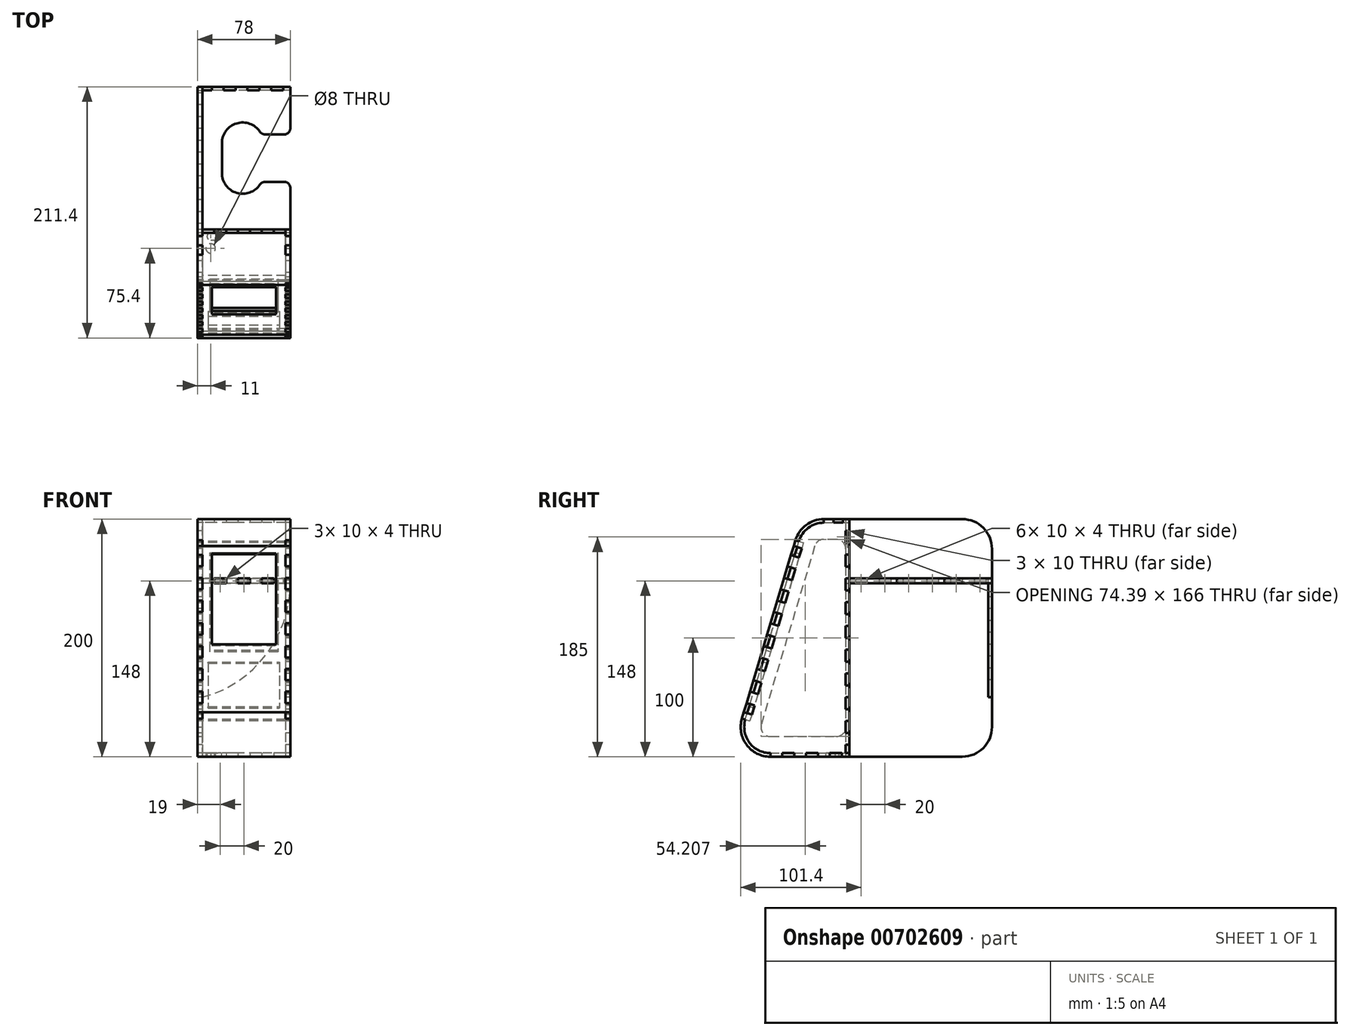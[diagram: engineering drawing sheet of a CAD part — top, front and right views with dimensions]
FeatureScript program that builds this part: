
annotation { "Feature Type Name" : "Feature", "Feature Type Description" : "" }
export const myFeature = defineFeature(function(context is Context, id is Id, definition is map)
    precondition{}
    {
        {
            var Q0;
            Q0=qCreatedBy(makeId("Right.planeOp"),FACE);
            var sketch = newSketch(context, id + "F0", { "sketchPlane" : qUnion([Q0])});
            skLineSegment(sketch, "E0", {"start": v(0, 0) * mm, "end": v(-66.4, 0) * mm});
            skLineSegment(sketch, "E1", {"start": v(-90.34, 32.18) * mm, "end": v(-87.13, 42.92) * mm});
            skLineSegment(sketch, "E2", {"start": v(-21.4, 200) * mm, "end": v(0, 200) * mm});
            skLineSegment(sketch, "E3", {"start": v(0, 200) * mm, "end": v(0, 0) * mm});
            skLineSegment(sketch, "E4", {"start": v(0, 0) * mm, "end": v(95, 0) * mm});
            skLineSegment(sketch, "E5", {"start": v(120, 25) * mm, "end": v(120, 175) * mm});
            skLineSegment(sketch, "E6", {"start": v(95, 200) * mm, "end": v(0, 200) * mm});
            skLineSegment(sketch, "E7", {"start": v(-48.22, 172.6) * mm, "end": v(-45.34, 182.18) * mm});
            skLineSegment(sketch, "E8", {"start": v(-72.93, 90.23) * mm, "end": v(-48.22, 172.6) * mm});
            skPoint(sketch, "E9.visualSharp", {"position": v(-40, 200) * mm});
            skArc(sketch, "E9.filletArc", {"start": v(-21.4, 200) * mm, "mid": v(-36.32, 195.06) * mm, "end": v(-45.34, 182.18) * mm});
            skPoint(sketch, "E10.visualSharp", {"position": v(-100, 0) * mm});
            skArc(sketch, "E10.filletArc", {"start": v(-90.34, 32.18) * mm, "mid": v(-86.46, 10.08) * mm, "end": v(-66.4, 0) * mm});
            skLineSegment(sketch, "E11", {"start": v(-75.8, 80.65) * mm, "end": v(-72.93, 90.23) * mm});
            skLineSegment(sketch, "E12", {"start": v(-87.13, 42.92) * mm, "end": v(-75.8, 80.65) * mm});
            skPoint(sketch, "E13.visualSharp", {"position": v(120, 200) * mm});
            skArc(sketch, "E13.filletArc", {"start": v(120, 175) * mm, "mid": v(112.68, 192.68) * mm, "end": v(95, 200) * mm});
            skPoint(sketch, "E14.visualSharp", {"position": v(120, 0) * mm});
            skArc(sketch, "E14.filletArc", {"start": v(95, 0) * mm, "mid": v(112.68, 7.32) * mm, "end": v(120, 25) * mm});
            skArc(sketch, "E15.0", {"start": v(-87.47, 31.32) * mm, "mid": v(-84.05, 11.87) * mm, "end": v(-66.4, 3) * mm});
            skLineSegment(sketch, "E15.1", {"start": v(-3, 3) * mm, "end": v(-66.4, 3) * mm});
            skLineSegment(sketch, "E15.2", {"start": v(-87.47, 31.32) * mm, "end": v(-84.25, 42.06) * mm});
            skLineSegment(sketch, "E15.3", {"start": v(-3, 197) * mm, "end": v(-3, 3) * mm});
            skLineSegment(sketch, "E15.4", {"start": v(-21.4, 197) * mm, "end": v(-3, 197) * mm});
            skArc(sketch, "E15.5", {"start": v(-21.4, 197) * mm, "mid": v(-34.53, 192.65) * mm, "end": v(-42.47, 181.32) * mm});
            skLineSegment(sketch, "E15.6", {"start": v(-84.25, 42.06) * mm, "end": v(-72.93, 79.8) * mm});
            skLineSegment(sketch, "E15.7", {"start": v(-72.93, 79.8) * mm, "end": v(-70.06, 89.37) * mm});
            skLineSegment(sketch, "E15.8", {"start": v(-70.06, 89.37) * mm, "end": v(-45.34, 171.75) * mm});
            skLineSegment(sketch, "E15.9", {"start": v(-45.34, 171.75) * mm, "end": v(-42.47, 181.32) * mm});
            skLineSegment(sketch, "E16", {"start": v(-43.9, 176.54) * mm, "end": v(-40.07, 175.4) * mm});
            skLineSegment(sketch, "E17", {"start": v(-88.74, 37.55) * mm, "end": v(-82.03, 35.55) * mm});
            skLineSegment(sketch, "E18", {"start": v(-3, 197) * mm, "end": v(0, 197) * mm});
            skLineSegment(sketch, "E19", {"start": v(-3, 3) * mm, "end": v(0, 3) * mm});
            skLineSegment(sketch, "E20", {"start": v(-42.47, 181.32) * mm, "end": v(-38.64, 180.17) * mm});
            skLineSegment(sketch, "E21", {"start": v(-38.64, 180.17) * mm, "end": v(-83.64, 30.17) * mm});
            skLineSegment(sketch, "E22", {"start": v(-87.47, 31.32) * mm, "end": v(-83.64, 30.17) * mm});
            skCircle(sketch, "E23", {"center": v(-21.4, 175) * mm, "radius": 2 * mm});
            skCircle(sketch, "E24", {"center": v(-66.4, 25) * mm, "radius": 2 * mm});
            skCircle(sketch, "E25", {"center": v(95, 175) * mm, "radius": 2 * mm});
            skCircle(sketch, "E26", {"center": v(95, 25) * mm, "radius": 2 * mm});
            skLineSegment(sketch, "E27", {"start": v(-3, 190) * mm, "end": v(0, 190) * mm});
            skLineSegment(sketch, "E28.0.1.0", {"start": v(-3, 180) * mm, "end": v(0, 180) * mm});
            skLineSegment(sketch, "E28.0.2.0", {"start": v(-3, 170) * mm, "end": v(0, 170) * mm});
            skLineSegment(sketch, "E28.0.3.0", {"start": v(-3, 160) * mm, "end": v(0, 160) * mm});
            skLineSegment(sketch, "E28.0.4.0", {"start": v(-3, 150) * mm, "end": v(0, 150) * mm});
            skLineSegment(sketch, "E28.0.5.0", {"start": v(-3, 140) * mm, "end": v(0, 140) * mm});
            skLineSegment(sketch, "E28.0.6.0", {"start": v(-3, 130) * mm, "end": v(0, 130) * mm});
            skLineSegment(sketch, "E28.0.7.0", {"start": v(-3, 120) * mm, "end": v(0, 120) * mm});
            skLineSegment(sketch, "E28.0.8.0", {"start": v(-3, 110) * mm, "end": v(0, 110) * mm});
            skLineSegment(sketch, "E28.0.9.0", {"start": v(-3, 100) * mm, "end": v(0, 100) * mm});
            skLineSegment(sketch, "E28.0.10.0", {"start": v(-3, 90) * mm, "end": v(0, 90) * mm});
            skLineSegment(sketch, "E28.0.11.0", {"start": v(-3, 80) * mm, "end": v(0, 80) * mm});
            skLineSegment(sketch, "E28.0.12.0", {"start": v(-3, 70) * mm, "end": v(0, 70) * mm});
            skLineSegment(sketch, "E28.0.13.0", {"start": v(-3, 60) * mm, "end": v(0, 60) * mm});
            skLineSegment(sketch, "E28.0.14.0", {"start": v(-3, 50) * mm, "end": v(0, 50) * mm});
            skLineSegment(sketch, "E28.0.15.0", {"start": v(-3, 40) * mm, "end": v(0, 40) * mm});
            skLineSegment(sketch, "E28.0.16.0", {"start": v(-3, 30) * mm, "end": v(0, 30) * mm});
            skLineSegment(sketch, "E28.0.17.0", {"start": v(-3, 20) * mm, "end": v(0, 20) * mm});
            skLineSegment(sketch, "E28.0.18.0", {"start": v(-3, 10) * mm, "end": v(0, 10) * mm});
            skLineSegment(sketch, "E28.direction1", {"start": v(-3, 190) * mm, "end": v(22, 190) * mm, "construction": true});
            skLineSegment(sketch, "E28.direction2", {"start": v(-3, 190) * mm, "end": v(-3, 180) * mm, "construction": true});
            skLineSegment(sketch, "E29", {"start": v(-45.34, 182.18) * mm, "end": v(-43.9, 181.75) * mm});
            skLineSegment(sketch, "E30", {"start": v(-21.4, 200) * mm, "end": v(-21.4, 198.5) * mm});
            skLineSegment(sketch, "E31", {"start": v(-13.4, 200) * mm, "end": v(-13.4, 197) * mm});
            skLineSegment(sketch, "E32", {"start": v(-5.4, 197) * mm, "end": v(-5.4, 200) * mm});
            skLineSegment(sketch, "E33", {"start": v(-45.34, 171.75) * mm, "end": v(-48.22, 172.6) * mm});
            skLineSegment(sketch, "E34", {"start": v(-3, 197) * mm, "end": v(-3, 200) * mm});
            skLineSegment(sketch, "E35", {"start": v(-3, 3) * mm, "end": v(-3, 0) * mm});
            skLineSegment(sketch, "E36", {"start": v(-49.08, 169.73) * mm, "end": v(-42.38, 167.72) * mm});
            skLineSegment(sketch, "E37.0.1.0", {"start": v(-51.95, 160.15) * mm, "end": v(-45.25, 158.14) * mm});
            skLineSegment(sketch, "E37.0.2.0", {"start": v(-54.83, 150.58) * mm, "end": v(-48.12, 148.56) * mm});
            skLineSegment(sketch, "E37.0.3.0", {"start": v(-57.7, 141) * mm, "end": v(-51, 138.99) * mm});
            skLineSegment(sketch, "E37.0.4.0", {"start": v(-57.7, 130.56) * mm, "end": v(-53.87, 129.4) * mm});
            skLineSegment(sketch, "E37.0.5.0", {"start": v(-63.45, 121.84) * mm, "end": v(-56.74, 119.83) * mm});
            skLineSegment(sketch, "E37.0.6.0", {"start": v(-66.32, 112.26) * mm, "end": v(-59.62, 110.25) * mm});
            skLineSegment(sketch, "E37.0.7.0", {"start": v(-69.2, 102.68) * mm, "end": v(-62.49, 100.67) * mm});
            skLineSegment(sketch, "E37.0.8.0", {"start": v(-72.07, 93.1) * mm, "end": v(-65.36, 91.1) * mm});
            skLineSegment(sketch, "E37.0.9.0", {"start": v(-74.94, 83.53) * mm, "end": v(-68.24, 81.52) * mm});
            skLineSegment(sketch, "E37.0.10.0", {"start": v(-77.82, 73.95) * mm, "end": v(-71.11, 71.94) * mm});
            skLineSegment(sketch, "E37.0.11.0", {"start": v(-80.69, 64.37) * mm, "end": v(-73.98, 62.36) * mm});
            skLineSegment(sketch, "E37.0.12.0", {"start": v(-83.56, 54.8) * mm, "end": v(-76.86, 52.78) * mm});
            skLineSegment(sketch, "E37.direction1", {"start": v(-49.08, 169.73) * mm, "end": v(-28.76, 167.45) * mm, "construction": true});
            skLineSegment(sketch, "E37.direction2", {"start": v(-49.08, 169.73) * mm, "end": v(-51.95, 160.15) * mm, "construction": true});
            skLineSegment(sketch, "E38", {"start": v(-90.34, 32.18) * mm, "end": v(-87.47, 31.32) * mm});
            skLineSegment(sketch, "E39", {"start": v(-87.13, 42.92) * mm, "end": v(-84.25, 42.06) * mm});
            skLineSegment(sketch, "E40", {"start": v(-87.3, 37.12) * mm, "end": v(-85, 44.78) * mm, "construction": true});
            skLineSegment(sketch, "E41", {"start": v(-45.34, 176.97) * mm, "end": v(-47.64, 169.3) * mm, "construction": true});
            skLineSegment(sketch, "E42.0.0.13", {"start": v(-86.44, 45.22) * mm, "end": v(-79.73, 43.2) * mm});
            skPoint(sketch, "E43.orphan", {"position": v(-46.2, 168.87) * mm});
            skPoint(sketch, "E44.orphan", {"position": v(-49.08, 159.3) * mm});
            skPoint(sketch, "E45.orphan", {"position": v(-51.95, 149.71) * mm});
            skPoint(sketch, "E46.orphan", {"position": v(-54.83, 140.14) * mm});
            skPoint(sketch, "E47.orphan", {"position": v(-60.57, 131.42) * mm});
            skPoint(sketch, "E48.orphan", {"position": v(-60.57, 120.98) * mm});
            skPoint(sketch, "E49.orphan", {"position": v(-63.45, 111.4) * mm});
            skPoint(sketch, "E50.orphan", {"position": v(-66.32, 101.82) * mm});
            skPoint(sketch, "E51.orphan", {"position": v(-69.2, 92.24) * mm});
            skPoint(sketch, "E52.orphan", {"position": v(-72.07, 82.67) * mm});
            skPoint(sketch, "E53.orphan", {"position": v(-74.94, 73.09) * mm});
            skPoint(sketch, "E54.orphan", {"position": v(-77.82, 63.5) * mm});
            skPoint(sketch, "E55.orphan", {"position": v(-80.69, 53.93) * mm});
            skPoint(sketch, "E56.orphan", {"position": v(-83.56, 44.35) * mm});
            skPoint(sketch, "E57.orphan", {"position": v(-85.86, 36.7) * mm});
            skPoint(sketch, "E58.orphan", {"position": v(-46.78, 177.4) * mm});
            skLineSegment(sketch, "E59", {"start": v(-43.9, 176.54) * mm, "end": v(-46.78, 177.4) * mm});
            skLineSegment(sketch, "E60", {"start": v(-60.57, 131.42) * mm, "end": v(-57.7, 130.56) * mm});
            skLineSegment(sketch, "E61", {"start": v(-66.4, 3) * mm, "end": v(-66.4, 0) * mm});
            skLineSegment(sketch, "E62", {"start": v(-56.4, 3) * mm, "end": v(-56.4, 0) * mm});
            skLineSegment(sketch, "E63", {"start": v(-46.4, 3) * mm, "end": v(-46.4, 0) * mm});
            skLineSegment(sketch, "E64", {"start": v(-36.4, 3) * mm, "end": v(-36.4, 0) * mm});
            skLineSegment(sketch, "E65", {"start": v(-26.4, 3) * mm, "end": v(-26.4, 0) * mm});
            skLineSegment(sketch, "E66", {"start": v(-16.4, 3) * mm, "end": v(-16.4, 0) * mm});
            skLineSegment(sketch, "E67", {"start": v(-6.4, 3) * mm, "end": v(-6.4, 0) * mm});
            skLineSegment(sketch, "E68.bottom", {"start": v(15, 150) * mm, "end": v(5, 150) * mm});
            skLineSegment(sketch, "E68.top", {"start": v(15, 146) * mm, "end": v(5, 146) * mm});
            skLineSegment(sketch, "E68.left", {"start": v(15, 150) * mm, "end": v(15, 146) * mm});
            skLineSegment(sketch, "E68.right", {"start": v(5, 150) * mm, "end": v(5, 146) * mm});
            skLineSegment(sketch, "E69.1.0.0", {"start": v(35, 150) * mm, "end": v(35, 146) * mm});
            skLineSegment(sketch, "E69.1.0.1", {"start": v(35, 150) * mm, "end": v(25, 150) * mm});
            skLineSegment(sketch, "E69.1.0.2", {"start": v(35, 146) * mm, "end": v(25, 146) * mm});
            skLineSegment(sketch, "E69.1.0.3", {"start": v(25, 150) * mm, "end": v(25, 146) * mm});
            skLineSegment(sketch, "E69.2.0.0", {"start": v(55, 150) * mm, "end": v(55, 146) * mm});
            skLineSegment(sketch, "E69.2.0.1", {"start": v(55, 150) * mm, "end": v(45, 150) * mm});
            skLineSegment(sketch, "E69.2.0.2", {"start": v(55, 146) * mm, "end": v(45, 146) * mm});
            skLineSegment(sketch, "E69.2.0.3", {"start": v(45, 150) * mm, "end": v(45, 146) * mm});
            skLineSegment(sketch, "E69.3.0.0", {"start": v(75, 150) * mm, "end": v(75, 146) * mm});
            skLineSegment(sketch, "E69.3.0.1", {"start": v(75, 150) * mm, "end": v(65, 150) * mm});
            skLineSegment(sketch, "E69.3.0.2", {"start": v(75, 146) * mm, "end": v(65, 146) * mm});
            skLineSegment(sketch, "E69.3.0.3", {"start": v(65, 150) * mm, "end": v(65, 146) * mm});
            skLineSegment(sketch, "E69.4.0.0", {"start": v(95, 150) * mm, "end": v(95, 146) * mm});
            skLineSegment(sketch, "E69.4.0.1", {"start": v(95, 150) * mm, "end": v(85, 150) * mm});
            skLineSegment(sketch, "E69.4.0.2", {"start": v(95, 146) * mm, "end": v(85, 146) * mm});
            skLineSegment(sketch, "E69.4.0.3", {"start": v(85, 150) * mm, "end": v(85, 146) * mm});
            skLineSegment(sketch, "E69.5.0.0", {"start": v(115, 150) * mm, "end": v(115, 146) * mm});
            skLineSegment(sketch, "E69.5.0.1", {"start": v(115, 150) * mm, "end": v(105, 150) * mm});
            skLineSegment(sketch, "E69.5.0.2", {"start": v(115, 146) * mm, "end": v(105, 146) * mm});
            skLineSegment(sketch, "E69.5.0.3", {"start": v(105, 150) * mm, "end": v(105, 146) * mm});
            skLineSegment(sketch, "E69.direction1", {"start": v(5, 146) * mm, "end": v(25, 146) * mm, "construction": true});
            skLineSegment(sketch, "E70", {"start": v(-43.9, 181.75) * mm, "end": v(-42.47, 181.32) * mm});
            skLineSegment(sketch, "E71", {"start": v(-21.4, 198.5) * mm, "end": v(-21.4, 197) * mm});
            skArc(sketch, "E72", {"start": v(-43.9, 181.75) * mm, "mid": v(-35.43, 193.85) * mm, "end": v(-21.4, 198.5) * mm, "construction": true});
            skArc(sketch, "E73", {"start": v(-66.4, 1.5) * mm, "mid": v(-85.25, 10.97) * mm, "end": v(-88.9, 31.75) * mm, "construction": true});
            skSolve(sketch);
        }
        {
            var Q0;
            {var subQ0=sQuery(id+"F0.wireOp",EDGE,"E37.0.6.0");var subQ1=sQuery(id+"F0.wireOp",EDGE,"E8");var subQ2=makeQuery(id+"F0.imprint","INTERSECT",VERTEX,{"derivedFrom":[subQ1,subQ0]});Q0=makeQuery(id+"F0.imprint","IMPRINT",FACE,{"disambiguationData":[TD([[makeQuery(id+"F0.imprint","IMPRINT",EDGE,{"disambiguationData":[TD([[subQ2,1.0]])],"derivedFrom":subQ1}),-1.0]])]});}
            var Q1;
            {var subQ0=sQuery(id+"F0.wireOp",EDGE,"E37.0.7.0");var subQ1=sQuery(id+"F0.wireOp",EDGE,"E15.8");var subQ2=makeQuery(id+"F0.imprint","INTERSECT",VERTEX,{"derivedFrom":[subQ1,subQ0]});Q1=makeQuery(id+"F0.imprint","IMPRINT",FACE,{"disambiguationData":[TD([[makeQuery(id+"F0.imprint","IMPRINT",EDGE,{"disambiguationData":[TD([[subQ2,-1.0]])],"derivedFrom":subQ1}),-1.0]])]});}
            var Q2;
            {var subQ0=sQuery(id+"F0.wireOp",EDGE,"E37.0.4.0");Q2=makeQuery(id+"F0.imprint","IMPRINT",FACE,{"disambiguationData":[TD([[makeQuery(id+"F0.imprint","IMPRINT",EDGE,{"derivedFrom":subQ0}),-1.0]])]});}
            var Q3;
            {var subQ0=sQuery(id+"F0.wireOp",EDGE,"E37.0.2.0");var subQ1=sQuery(id+"F0.wireOp",EDGE,"E8");var subQ2=makeQuery(id+"F0.imprint","INTERSECT",VERTEX,{"derivedFrom":[subQ1,subQ0]});Q3=makeQuery(id+"F0.imprint","IMPRINT",FACE,{"disambiguationData":[TD([[makeQuery(id+"F0.imprint","IMPRINT",EDGE,{"disambiguationData":[TD([[subQ2,1.0]])],"derivedFrom":subQ1}),-1.0]])]});}
            var Q4;
            {var subQ0=sQuery(id+"F0.wireOp",EDGE,"E37.0.3.0");var subQ1=sQuery(id+"F0.wireOp",EDGE,"E15.8");var subQ2=makeQuery(id+"F0.imprint","INTERSECT",VERTEX,{"derivedFrom":[subQ1,subQ0]});Q4=makeQuery(id+"F0.imprint","IMPRINT",FACE,{"disambiguationData":[TD([[makeQuery(id+"F0.imprint","IMPRINT",EDGE,{"disambiguationData":[TD([[subQ2,-1.0]])],"derivedFrom":subQ1}),-1.0]])]});}
            var Q5;
            {var subQ0=sQuery(id+"F0.wireOp",EDGE,"E36");var subQ1=sQuery(id+"F0.wireOp",EDGE,"E8");var subQ2=makeQuery(id+"F0.imprint","INTERSECT",VERTEX,{"derivedFrom":[subQ1,subQ0]});Q5=makeQuery(id+"F0.imprint","IMPRINT",FACE,{"disambiguationData":[TD([[makeQuery(id+"F0.imprint","IMPRINT",EDGE,{"disambiguationData":[TD([[subQ2,1.0]])],"derivedFrom":subQ1}),-1.0]])]});}
            var Q6;
            {var subQ0=sQuery(id+"F0.wireOp",EDGE,"E37.0.1.0");var subQ1=sQuery(id+"F0.wireOp",EDGE,"E15.8");var subQ2=makeQuery(id+"F0.imprint","INTERSECT",VERTEX,{"derivedFrom":[subQ1,subQ0]});Q6=makeQuery(id+"F0.imprint","IMPRINT",FACE,{"disambiguationData":[TD([[makeQuery(id+"F0.imprint","IMPRINT",EDGE,{"disambiguationData":[TD([[subQ2,-1.0]])],"derivedFrom":subQ1}),-1.0]])]});}
            var Q7;
            {var subQ0=sQuery(id+"F0.wireOp",EDGE,"E30");Q7=makeQuery(id+"F0.imprint","IMPRINT",FACE,{"disambiguationData":[TD([[makeQuery(id+"F0.imprint","IMPRINT",EDGE,{"derivedFrom":subQ0}),1.0]])]});}
            var Q8;
            {var subQ0=sQuery(id+"F0.wireOp",EDGE,"E18");Q8=makeQuery(id+"F0.imprint","IMPRINT",FACE,{"disambiguationData":[TD([[makeQuery(id+"F0.imprint","IMPRINT",EDGE,{"derivedFrom":subQ0}),-1.0]])]});}
            var Q9;
            {var subQ0=sQuery(id+"F0.wireOp",EDGE,"E28.0.1.0");Q9=makeQuery(id+"F0.imprint","IMPRINT",FACE,{"disambiguationData":[TD([[makeQuery(id+"F0.imprint","IMPRINT",EDGE,{"derivedFrom":subQ0}),-1.0]])]});}
            var Q10;
            {var subQ0=sQuery(id+"F0.wireOp",EDGE,"E28.0.3.0");Q10=makeQuery(id+"F0.imprint","IMPRINT",FACE,{"disambiguationData":[TD([[makeQuery(id+"F0.imprint","IMPRINT",EDGE,{"derivedFrom":subQ0}),-1.0]])]});}
            var Q11;
            {var subQ0=sQuery(id+"F0.wireOp",EDGE,"E28.0.5.0");Q11=makeQuery(id+"F0.imprint","IMPRINT",FACE,{"disambiguationData":[TD([[makeQuery(id+"F0.imprint","IMPRINT",EDGE,{"derivedFrom":subQ0}),-1.0]])]});}
            var Q12;
            {var subQ0=sQuery(id+"F0.wireOp",EDGE,"E28.0.7.0");Q12=makeQuery(id+"F0.imprint","IMPRINT",FACE,{"disambiguationData":[TD([[makeQuery(id+"F0.imprint","IMPRINT",EDGE,{"derivedFrom":subQ0}),-1.0]])]});}
            var Q13;
            {var subQ0=sQuery(id+"F0.wireOp",EDGE,"E28.0.9.0");Q13=makeQuery(id+"F0.imprint","IMPRINT",FACE,{"disambiguationData":[TD([[makeQuery(id+"F0.imprint","IMPRINT",EDGE,{"derivedFrom":subQ0}),-1.0]])]});}
            var Q14;
            {var subQ0=sQuery(id+"F0.wireOp",EDGE,"E28.0.11.0");Q14=makeQuery(id+"F0.imprint","IMPRINT",FACE,{"disambiguationData":[TD([[makeQuery(id+"F0.imprint","IMPRINT",EDGE,{"derivedFrom":subQ0}),-1.0]])]});}
            var Q15;
            {var subQ0=sQuery(id+"F0.wireOp",EDGE,"E28.0.13.0");Q15=makeQuery(id+"F0.imprint","IMPRINT",FACE,{"disambiguationData":[TD([[makeQuery(id+"F0.imprint","IMPRINT",EDGE,{"derivedFrom":subQ0}),-1.0]])]});}
            var Q16;
            {var subQ0=sQuery(id+"F0.wireOp",EDGE,"E28.0.15.0");Q16=makeQuery(id+"F0.imprint","IMPRINT",FACE,{"disambiguationData":[TD([[makeQuery(id+"F0.imprint","IMPRINT",EDGE,{"derivedFrom":subQ0}),-1.0]])]});}
            var Q17;
            {var subQ0=sQuery(id+"F0.wireOp",EDGE,"E28.0.17.0");Q17=makeQuery(id+"F0.imprint","IMPRINT",FACE,{"disambiguationData":[TD([[makeQuery(id+"F0.imprint","IMPRINT",EDGE,{"derivedFrom":subQ0}),-1.0]])]});}
            var Q18;
            {var subQ1=sQuery(id+"F0.wireOp",EDGE,"E4");Q18=makeQuery(id+"F0.imprint","IMPRINT",FACE,{"disambiguationData":[TD([[makeQuery(id+"F0.imprint","IMPRINT",EDGE,{"derivedFrom":subQ1}),1.0]])]});}
            var Q19;
            {var subQ18=sQuery(id+"F0.wireOp",EDGE,"E15.0");Q19=makeQuery(id+"F0.imprint","IMPRINT",FACE,{"disambiguationData":[TD([[makeQuery(id+"F0.imprint","IMPRINT",EDGE,{"derivedFrom":subQ18}),1.0]])]});}
            var Q20;
            {var subQ2=sQuery(id+"F0.wireOp",EDGE,"E16");Q20=makeQuery(id+"F0.imprint","IMPRINT",FACE,{"disambiguationData":[TD([[makeQuery(id+"F0.imprint","IMPRINT",EDGE,{"derivedFrom":subQ2}),1.0]])]});}
            var Q21;
            {var subQ4=sQuery(id+"F0.wireOp",EDGE,"E19");Q21=makeQuery(id+"F0.imprint","IMPRINT",FACE,{"disambiguationData":[TD([[makeQuery(id+"F0.imprint","IMPRINT",EDGE,{"derivedFrom":subQ4}),-1.0]])]});}
            var Q22;
            {var subQ4=sQuery(id+"F0.wireOp",EDGE,"E18");Q22=makeQuery(id+"F0.imprint","IMPRINT",FACE,{"disambiguationData":[TD([[makeQuery(id+"F0.imprint","IMPRINT",EDGE,{"derivedFrom":subQ4}),1.0]])]});}
            var Q23;
            {var subQ0=sQuery(id+"F0.wireOp",EDGE,"E32");Q23=makeQuery(id+"F0.imprint","IMPRINT",FACE,{"disambiguationData":[TD([[makeQuery(id+"F0.imprint","IMPRINT",EDGE,{"derivedFrom":subQ0}),-1.0]])]});}
            var Q24;
            {var subQ3=sQuery(id+"F0.wireOp",EDGE,"E15.8");var subQ7=sQuery(id+"F0.wireOp",EDGE,"E15.7");var subQ8=makeQuery(id+"F0.imprint","INTERSECT",VERTEX,{"derivedFrom":[subQ7,subQ3]});Q24=makeQuery(id+"F0.imprint","IMPRINT",FACE,{"disambiguationData":[TD([[makeQuery(id+"F0.imprint","IMPRINT",EDGE,{"disambiguationData":[TD([[subQ8,1.0]])],"derivedFrom":subQ7}),-1.0]])]});}
            var Q25;
            {var subQ0=sQuery(id+"F0.wireOp",EDGE,"E37.0.10.0");var subQ1=sQuery(id+"F0.wireOp",EDGE,"E12");var subQ2=makeQuery(id+"F0.imprint","INTERSECT",VERTEX,{"derivedFrom":[subQ1,subQ0]});Q25=makeQuery(id+"F0.imprint","IMPRINT",FACE,{"disambiguationData":[TD([[makeQuery(id+"F0.imprint","IMPRINT",EDGE,{"disambiguationData":[TD([[subQ2,1.0]])],"derivedFrom":subQ1}),-1.0]])]});}
            var Q26;
            {var subQ0=sQuery(id+"F0.wireOp",EDGE,"E37.0.11.0");var subQ1=sQuery(id+"F0.wireOp",EDGE,"E15.6");var subQ2=makeQuery(id+"F0.imprint","INTERSECT",VERTEX,{"derivedFrom":[subQ1,subQ0]});Q26=makeQuery(id+"F0.imprint","IMPRINT",FACE,{"disambiguationData":[TD([[makeQuery(id+"F0.imprint","IMPRINT",EDGE,{"disambiguationData":[TD([[subQ2,-1.0]])],"derivedFrom":subQ1}),-1.0]])]});}
            var Q27;
            {var subQ0=sQuery(id+"F0.wireOp",EDGE,"E37.0.12.0");var subQ1=sQuery(id+"F0.wireOp",EDGE,"E12");var subQ2=makeQuery(id+"F0.imprint","INTERSECT",VERTEX,{"derivedFrom":[subQ1,subQ0]});Q27=makeQuery(id+"F0.imprint","IMPRINT",FACE,{"disambiguationData":[TD([[makeQuery(id+"F0.imprint","IMPRINT",EDGE,{"disambiguationData":[TD([[subQ2,1.0]])],"derivedFrom":subQ1}),-1.0]])]});}
            var Q28;
            {var subQ0=sQuery(id+"F0.wireOp",EDGE,"E42.0.0.13");var subQ1=sQuery(id+"F0.wireOp",EDGE,"E15.6");var subQ2=makeQuery(id+"F0.imprint","INTERSECT",VERTEX,{"derivedFrom":[subQ1,subQ0]});Q28=makeQuery(id+"F0.imprint","IMPRINT",FACE,{"disambiguationData":[TD([[makeQuery(id+"F0.imprint","IMPRINT",EDGE,{"disambiguationData":[TD([[subQ2,-1.0]])],"derivedFrom":subQ1}),-1.0]])]});}
            var Q29;
            {var subQ0=sQuery(id+"F0.wireOp",EDGE,"E38");Q29=makeQuery(id+"F0.imprint","IMPRINT",FACE,{"disambiguationData":[TD([[makeQuery(id+"F0.imprint","IMPRINT",EDGE,{"derivedFrom":subQ0}),1.0]])]});}
            var Q30;
            {var subQ0=sQuery(id+"F0.wireOp",EDGE,"E22");Q30=makeQuery(id+"F0.imprint","IMPRINT",FACE,{"disambiguationData":[TD([[makeQuery(id+"F0.imprint","IMPRINT",EDGE,{"derivedFrom":subQ0}),1.0]])]});}
            var Q31;
            {var subQ0=sQuery(id+"F0.wireOp",EDGE,"E29");Q31=makeQuery(id+"F0.imprint","IMPRINT",FACE,{"disambiguationData":[TD([[makeQuery(id+"F0.imprint","IMPRINT",EDGE,{"derivedFrom":subQ0}),-1.0]])]});}
            var Q32;
            {var subQ3=sQuery(id+"F0.wireOp",EDGE,"E60");Q32=makeQuery(id+"F0.imprint","IMPRINT",FACE,{"disambiguationData":[TD([[makeQuery(id+"F0.imprint","IMPRINT",EDGE,{"derivedFrom":subQ3}),-1.0]])]});}
            var Q33;
            {var subQ7=sQuery(id+"F0.wireOp",EDGE,"E11");var subQ8=sQuery(id+"F0.wireOp",EDGE,"E8");var subQ9=makeQuery(id+"F0.imprint","INTERSECT",VERTEX,{"derivedFrom":[subQ8,subQ7]});Q33=makeQuery(id+"F0.imprint","IMPRINT",FACE,{"disambiguationData":[TD([[makeQuery(id+"F0.imprint","IMPRINT",EDGE,{"disambiguationData":[TD([[subQ9,-1.0]])],"derivedFrom":subQ8}),-1.0]])]});}
            var Q34;
            {var subQ0=sQuery(id+"F0.wireOp",EDGE,"E35");Q34=makeQuery(id+"F0.imprint","IMPRINT",FACE,{"disambiguationData":[TD([[makeQuery(id+"F0.imprint","IMPRINT",EDGE,{"derivedFrom":subQ0}),-1.0]])]});}
            var Q35;
            {var subQ0=sQuery(id+"F0.wireOp",EDGE,"E65");Q35=makeQuery(id+"F0.imprint","IMPRINT",FACE,{"disambiguationData":[TD([[makeQuery(id+"F0.imprint","IMPRINT",EDGE,{"derivedFrom":subQ0}),1.0]])]});}
            var Q36;
            {var subQ0=sQuery(id+"F0.wireOp",EDGE,"E63");Q36=makeQuery(id+"F0.imprint","IMPRINT",FACE,{"disambiguationData":[TD([[makeQuery(id+"F0.imprint","IMPRINT",EDGE,{"derivedFrom":subQ0}),1.0]])]});}
            var Q37;
            {var subQ0=sQuery(id+"F0.wireOp",EDGE,"E61");Q37=makeQuery(id+"F0.imprint","IMPRINT",FACE,{"disambiguationData":[TD([[makeQuery(id+"F0.imprint","IMPRINT",EDGE,{"derivedFrom":subQ0}),1.0]])]});}
            var Q38;
            Q38=makeQuery(id+"F0.imprint","IMPRINT",FACE,{"disambiguationData":[TD([[makeQuery(id+"F0.imprint","IMPRINT",EDGE,{"derivedFrom":sQuery(id+"F0.wireOp",EDGE,"E23")}),1.0]])]});
            var Q39;
            Q39=makeQuery(id+"F0.imprint","IMPRINT",FACE,{"disambiguationData":[TD([[makeQuery(id+"F0.imprint","IMPRINT",EDGE,{"derivedFrom":sQuery(id+"F0.wireOp",EDGE,"E24")}),1.0]])]});
            var Q40;
            Q40=makeQuery(id+"F0.imprint","IMPRINT",FACE,{"disambiguationData":[TD([[makeQuery(id+"F0.imprint","IMPRINT",EDGE,{"derivedFrom":sQuery(id+"F0.wireOp",EDGE,"E26")}),1.0]])]});
            var Q41;
            Q41=makeQuery(id+"F0.imprint","IMPRINT",FACE,{"disambiguationData":[TD([[makeQuery(id+"F0.imprint","IMPRINT",EDGE,{"derivedFrom":sQuery(id+"F0.wireOp",EDGE,"E25")}),1.0]])]});
            extrude(context, id + "F1", {"entities" : qUnion([Q0, Q1, Q2, Q3, Q4, Q5, Q6, Q7, Q8, Q9, Q10, Q11, Q12, Q13, Q14, Q15, Q16, Q17, Q18, Q19, Q20, Q21, Q22, Q23, Q24, Q25, Q26, Q27, Q28, Q29, Q30, Q31, Q32, Q33, Q34, Q35, Q36, Q37, Q38, Q39, Q40, Q41]), "depth" : 4 * mm, "offsetDistance" : 25 * mm});
        }
        {
            var Q0;
            Q0=makeQuery(id+"F0.imprint","IMPRINT",FACE,{"disambiguationData":[TD([[makeQuery(id+"F0.imprint","IMPRINT",EDGE,{"derivedFrom":sQuery(id+"F0.wireOp",EDGE,"E15.3")}),1.0]])]});
            var Q1;
            {var subQ4=sQuery(id+"F0.wireOp",EDGE,"E18");Q1=makeQuery(id+"F0.imprint","IMPRINT",FACE,{"disambiguationData":[TD([[makeQuery(id+"F0.imprint","IMPRINT",EDGE,{"derivedFrom":subQ4}),1.0]])]});}
            var Q2;
            {var subQ4=sQuery(id+"F0.wireOp",EDGE,"E19");Q2=makeQuery(id+"F0.imprint","IMPRINT",FACE,{"disambiguationData":[TD([[makeQuery(id+"F0.imprint","IMPRINT",EDGE,{"derivedFrom":subQ4}),-1.0]])]});}
            extrude(context, id + "F2", {"entities" : qUnion([Q0, Q1, Q2]), "depth" : 78 * mm, "offsetDistance" : 25 * mm});
        }
        {
            var Q0;
            {var subQ0=sQuery(id+"F0.wireOp",EDGE,"E38");Q0=makeQuery(id+"F0.imprint","IMPRINT",FACE,{"disambiguationData":[TD([[makeQuery(id+"F0.imprint","IMPRINT",EDGE,{"derivedFrom":subQ0}),1.0]])]});}
            var Q1;
            {var subQ0=sQuery(id+"F0.wireOp",EDGE,"E30");Q1=makeQuery(id+"F0.imprint","IMPRINT",FACE,{"disambiguationData":[TD([[makeQuery(id+"F0.imprint","IMPRINT",EDGE,{"derivedFrom":subQ0}),1.0]])]});}
            var Q2;
            {var subQ0=sQuery(id+"F0.wireOp",EDGE,"E31");Q2=makeQuery(id+"F0.imprint","IMPRINT",FACE,{"disambiguationData":[TD([[makeQuery(id+"F0.imprint","IMPRINT",EDGE,{"derivedFrom":subQ0}),1.0]])]});}
            var Q3;
            {var subQ0=sQuery(id+"F0.wireOp",EDGE,"E32");Q3=makeQuery(id+"F0.imprint","IMPRINT",FACE,{"disambiguationData":[TD([[makeQuery(id+"F0.imprint","IMPRINT",EDGE,{"derivedFrom":subQ0}),-1.0]])]});}
            var Q4;
            {var subQ4=sQuery(id+"F0.wireOp",EDGE,"E18");Q4=makeQuery(id+"F0.imprint","IMPRINT",FACE,{"disambiguationData":[TD([[makeQuery(id+"F0.imprint","IMPRINT",EDGE,{"derivedFrom":subQ4}),1.0]])]});}
            var Q5;
            {var subQ4=sQuery(id+"F0.wireOp",EDGE,"E19");Q5=makeQuery(id+"F0.imprint","IMPRINT",FACE,{"disambiguationData":[TD([[makeQuery(id+"F0.imprint","IMPRINT",EDGE,{"derivedFrom":subQ4}),-1.0]])]});}
            var Q6;
            Q6=makeQuery(id+"F0.imprint","IMPRINT",FACE,{"disambiguationData":[TD([[makeQuery(id+"F0.imprint","IMPRINT",EDGE,{"derivedFrom":sQuery(id+"F0.wireOp",EDGE,"E9.filletArc")}),1.0]])]});
            var Q7;
            {var subQ0=sQuery(id+"F0.wireOp",EDGE,"E10.filletArc");Q7=makeQuery(id+"F0.imprint","IMPRINT",FACE,{"disambiguationData":[TD([[makeQuery(id+"F0.imprint","IMPRINT",EDGE,{"derivedFrom":subQ0}),1.0]])]});}
            var Q8;
            {var subQ0=sQuery(id+"F0.wireOp",EDGE,"E29");Q8=makeQuery(id+"F0.imprint","IMPRINT",FACE,{"disambiguationData":[TD([[makeQuery(id+"F0.imprint","IMPRINT",EDGE,{"derivedFrom":subQ0}),-1.0]])]});}
            var Q9;
            {var subQ0=sQuery(id+"F0.wireOp",EDGE,"E35");Q9=makeQuery(id+"F0.imprint","IMPRINT",FACE,{"disambiguationData":[TD([[makeQuery(id+"F0.imprint","IMPRINT",EDGE,{"derivedFrom":subQ0}),-1.0]])]});}
            var Q10;
            {var subQ0=sQuery(id+"F0.wireOp",EDGE,"E66");Q10=makeQuery(id+"F0.imprint","IMPRINT",FACE,{"disambiguationData":[TD([[makeQuery(id+"F0.imprint","IMPRINT",EDGE,{"derivedFrom":subQ0}),1.0]])]});}
            var Q11;
            {var subQ0=sQuery(id+"F0.wireOp",EDGE,"E65");Q11=makeQuery(id+"F0.imprint","IMPRINT",FACE,{"disambiguationData":[TD([[makeQuery(id+"F0.imprint","IMPRINT",EDGE,{"derivedFrom":subQ0}),1.0]])]});}
            var Q12;
            {var subQ0=sQuery(id+"F0.wireOp",EDGE,"E64");Q12=makeQuery(id+"F0.imprint","IMPRINT",FACE,{"disambiguationData":[TD([[makeQuery(id+"F0.imprint","IMPRINT",EDGE,{"derivedFrom":subQ0}),1.0]])]});}
            var Q13;
            {var subQ0=sQuery(id+"F0.wireOp",EDGE,"E63");Q13=makeQuery(id+"F0.imprint","IMPRINT",FACE,{"disambiguationData":[TD([[makeQuery(id+"F0.imprint","IMPRINT",EDGE,{"derivedFrom":subQ0}),1.0]])]});}
            var Q14;
            {var subQ0=sQuery(id+"F0.wireOp",EDGE,"E62");Q14=makeQuery(id+"F0.imprint","IMPRINT",FACE,{"disambiguationData":[TD([[makeQuery(id+"F0.imprint","IMPRINT",EDGE,{"derivedFrom":subQ0}),1.0]])]});}
            var Q15;
            {var subQ0=sQuery(id+"F0.wireOp",EDGE,"E61");Q15=makeQuery(id+"F0.imprint","IMPRINT",FACE,{"disambiguationData":[TD([[makeQuery(id+"F0.imprint","IMPRINT",EDGE,{"derivedFrom":subQ0}),1.0]])]});}
            extrude(context, id + "F3", {"entities" : qUnion([Q0, Q1, Q2, Q3, Q4, Q5, Q6, Q7, Q8, Q9, Q10, Q11, Q12, Q13, Q14, Q15]), "depth" : 78 * mm, "offsetDistance" : 25 * mm});
        }
        {
            var Q0;
            {var subQ0=sQuery(id+"F0.wireOp",EDGE,"E37.0.10.0");var subQ1=sQuery(id+"F0.wireOp",EDGE,"E12");var subQ2=makeQuery(id+"F0.imprint","INTERSECT",VERTEX,{"derivedFrom":[subQ1,subQ0]});Q0=makeQuery(id+"F0.imprint","IMPRINT",FACE,{"disambiguationData":[TD([[makeQuery(id+"F0.imprint","IMPRINT",EDGE,{"disambiguationData":[TD([[subQ2,1.0]])],"derivedFrom":subQ1}),-1.0]])]});}
            var Q1;
            {var subQ0=sQuery(id+"F0.wireOp",EDGE,"E37.0.7.0");var subQ1=sQuery(id+"F0.wireOp",EDGE,"E8");var subQ2=makeQuery(id+"F0.imprint","INTERSECT",VERTEX,{"derivedFrom":[subQ1,subQ0]});Q1=makeQuery(id+"F0.imprint","IMPRINT",FACE,{"disambiguationData":[TD([[makeQuery(id+"F0.imprint","IMPRINT",EDGE,{"disambiguationData":[TD([[subQ2,1.0]])],"derivedFrom":subQ1}),-1.0]])]});}
            var Q2;
            {var subQ0=sQuery(id+"F0.wireOp",EDGE,"E37.0.6.0");var subQ1=sQuery(id+"F0.wireOp",EDGE,"E8");var subQ2=makeQuery(id+"F0.imprint","INTERSECT",VERTEX,{"derivedFrom":[subQ1,subQ0]});Q2=makeQuery(id+"F0.imprint","IMPRINT",FACE,{"disambiguationData":[TD([[makeQuery(id+"F0.imprint","IMPRINT",EDGE,{"disambiguationData":[TD([[subQ2,1.0]])],"derivedFrom":subQ1}),-1.0]])]});}
            var Q3;
            {var subQ0=sQuery(id+"F0.wireOp",EDGE,"E37.0.5.0");var subQ1=sQuery(id+"F0.wireOp",EDGE,"E8");var subQ2=makeQuery(id+"F0.imprint","INTERSECT",VERTEX,{"derivedFrom":[subQ1,subQ0]});Q3=makeQuery(id+"F0.imprint","IMPRINT",FACE,{"disambiguationData":[TD([[makeQuery(id+"F0.imprint","IMPRINT",EDGE,{"disambiguationData":[TD([[subQ2,1.0]])],"derivedFrom":subQ1}),-1.0]])]});}
            var Q4;
            {var subQ3=sQuery(id+"F0.wireOp",EDGE,"E60");Q4=makeQuery(id+"F0.imprint","IMPRINT",FACE,{"disambiguationData":[TD([[makeQuery(id+"F0.imprint","IMPRINT",EDGE,{"derivedFrom":subQ3}),-1.0]])]});}
            var Q5;
            {var subQ3=sQuery(id+"F0.wireOp",EDGE,"E60");Q5=makeQuery(id+"F0.imprint","IMPRINT",FACE,{"disambiguationData":[TD([[makeQuery(id+"F0.imprint","IMPRINT",EDGE,{"derivedFrom":subQ3}),1.0]])]});}
            var Q6;
            {var subQ0=sQuery(id+"F0.wireOp",EDGE,"E37.0.2.0");var subQ1=sQuery(id+"F0.wireOp",EDGE,"E8");var subQ2=makeQuery(id+"F0.imprint","INTERSECT",VERTEX,{"derivedFrom":[subQ1,subQ0]});Q6=makeQuery(id+"F0.imprint","IMPRINT",FACE,{"disambiguationData":[TD([[makeQuery(id+"F0.imprint","IMPRINT",EDGE,{"disambiguationData":[TD([[subQ2,1.0]])],"derivedFrom":subQ1}),-1.0]])]});}
            var Q7;
            {var subQ0=sQuery(id+"F0.wireOp",EDGE,"E37.0.1.0");var subQ1=sQuery(id+"F0.wireOp",EDGE,"E8");var subQ2=makeQuery(id+"F0.imprint","INTERSECT",VERTEX,{"derivedFrom":[subQ1,subQ0]});Q7=makeQuery(id+"F0.imprint","IMPRINT",FACE,{"disambiguationData":[TD([[makeQuery(id+"F0.imprint","IMPRINT",EDGE,{"disambiguationData":[TD([[subQ2,1.0]])],"derivedFrom":subQ1}),-1.0]])]});}
            var Q8;
            {var subQ0=sQuery(id+"F0.wireOp",EDGE,"E36");var subQ1=sQuery(id+"F0.wireOp",EDGE,"E8");var subQ2=makeQuery(id+"F0.imprint","INTERSECT",VERTEX,{"derivedFrom":[subQ1,subQ0]});Q8=makeQuery(id+"F0.imprint","IMPRINT",FACE,{"disambiguationData":[TD([[makeQuery(id+"F0.imprint","IMPRINT",EDGE,{"disambiguationData":[TD([[subQ2,1.0]])],"derivedFrom":subQ1}),-1.0]])]});}
            var Q9;
            {var subQ0=sQuery(id+"F0.wireOp",EDGE,"E33");Q9=makeQuery(id+"F0.imprint","IMPRINT",FACE,{"disambiguationData":[TD([[makeQuery(id+"F0.imprint","IMPRINT",EDGE,{"derivedFrom":subQ0}),1.0]])]});}
            var Q10;
            {var subQ0=sQuery(id+"F0.wireOp",EDGE,"E37.0.11.0");var subQ1=sQuery(id+"F0.wireOp",EDGE,"E12");var subQ2=makeQuery(id+"F0.imprint","INTERSECT",VERTEX,{"derivedFrom":[subQ1,subQ0]});Q10=makeQuery(id+"F0.imprint","IMPRINT",FACE,{"disambiguationData":[TD([[makeQuery(id+"F0.imprint","IMPRINT",EDGE,{"disambiguationData":[TD([[subQ2,1.0]])],"derivedFrom":subQ1}),-1.0]])]});}
            var Q11;
            {var subQ0=sQuery(id+"F0.wireOp",EDGE,"E37.0.12.0");var subQ1=sQuery(id+"F0.wireOp",EDGE,"E12");var subQ2=makeQuery(id+"F0.imprint","INTERSECT",VERTEX,{"derivedFrom":[subQ1,subQ0]});Q11=makeQuery(id+"F0.imprint","IMPRINT",FACE,{"disambiguationData":[TD([[makeQuery(id+"F0.imprint","IMPRINT",EDGE,{"disambiguationData":[TD([[subQ2,1.0]])],"derivedFrom":subQ1}),-1.0]])]});}
            var Q12;
            {var subQ0=sQuery(id+"F0.wireOp",EDGE,"E39");Q12=makeQuery(id+"F0.imprint","IMPRINT",FACE,{"disambiguationData":[TD([[makeQuery(id+"F0.imprint","IMPRINT",EDGE,{"derivedFrom":subQ0}),1.0]])]});}
            var Q13;
            {var subQ0=sQuery(id+"F0.wireOp",EDGE,"E39");Q13=makeQuery(id+"F0.imprint","IMPRINT",FACE,{"disambiguationData":[TD([[makeQuery(id+"F0.imprint","IMPRINT",EDGE,{"derivedFrom":subQ0}),-1.0]])]});}
            var Q14;
            {var subQ0=sQuery(id+"F0.wireOp",EDGE,"E33");Q14=makeQuery(id+"F0.imprint","IMPRINT",FACE,{"disambiguationData":[TD([[makeQuery(id+"F0.imprint","IMPRINT",EDGE,{"derivedFrom":subQ0}),-1.0]])]});}
            var Q15;
            {var subQ7=sQuery(id+"F0.wireOp",EDGE,"E12");var subQ9=sQuery(id+"F0.wireOp",EDGE,"E11");var subQ10=makeQuery(id+"F0.imprint","INTERSECT",VERTEX,{"derivedFrom":[subQ9,subQ7]});Q15=makeQuery(id+"F0.imprint","IMPRINT",FACE,{"disambiguationData":[TD([[makeQuery(id+"F0.imprint","IMPRINT",EDGE,{"disambiguationData":[TD([[subQ10,-1.0]])],"derivedFrom":subQ9}),-1.0]])]});}
            var Q16;
            {var subQ5=sQuery(id+"F0.wireOp",EDGE,"E11");var subQ6=sQuery(id+"F0.wireOp",EDGE,"E8");var subQ7=makeQuery(id+"F0.imprint","INTERSECT",VERTEX,{"derivedFrom":[subQ6,subQ5]});Q16=makeQuery(id+"F0.imprint","IMPRINT",FACE,{"disambiguationData":[TD([[makeQuery(id+"F0.imprint","IMPRINT",EDGE,{"disambiguationData":[TD([[subQ7,-1.0]])],"derivedFrom":subQ6}),-1.0]])]});}
            extrude(context, id + "F4", {"entities" : qUnion([Q0, Q1, Q2, Q3, Q4, Q5, Q6, Q7, Q8, Q9, Q10, Q11, Q12, Q13, Q14, Q15, Q16]), "depth" : 78 * mm, "offsetDistance" : 25 * mm});
        }
        {
            var Q0;
            {var subQ0=sQuery(id+"F0.wireOp",EDGE,"E20");Q0=makeQuery(id+"F0.imprint","IMPRINT",FACE,{"disambiguationData":[TD([[makeQuery(id+"F0.imprint","IMPRINT",EDGE,{"derivedFrom":subQ0}),-1.0]])]});}
            var Q1;
            {var subQ0=sQuery(id+"F0.wireOp",EDGE,"E16");Q1=makeQuery(id+"F0.imprint","IMPRINT",FACE,{"disambiguationData":[TD([[makeQuery(id+"F0.imprint","IMPRINT",EDGE,{"derivedFrom":subQ0}),-1.0]])]});}
            var Q2;
            {var subQ0=sQuery(id+"F0.wireOp",EDGE,"E37.0.1.0");var subQ1=sQuery(id+"F0.wireOp",EDGE,"E15.8");var subQ2=makeQuery(id+"F0.imprint","INTERSECT",VERTEX,{"derivedFrom":[subQ1,subQ0]});Q2=makeQuery(id+"F0.imprint","IMPRINT",FACE,{"disambiguationData":[TD([[makeQuery(id+"F0.imprint","IMPRINT",EDGE,{"disambiguationData":[TD([[subQ2,-1.0]])],"derivedFrom":subQ1}),-1.0]])]});}
            var Q3;
            {var subQ0=sQuery(id+"F0.wireOp",EDGE,"E37.0.2.0");var subQ1=sQuery(id+"F0.wireOp",EDGE,"E15.8");var subQ2=makeQuery(id+"F0.imprint","INTERSECT",VERTEX,{"derivedFrom":[subQ1,subQ0]});Q3=makeQuery(id+"F0.imprint","IMPRINT",FACE,{"disambiguationData":[TD([[makeQuery(id+"F0.imprint","IMPRINT",EDGE,{"disambiguationData":[TD([[subQ2,-1.0]])],"derivedFrom":subQ1}),-1.0]])]});}
            var Q4;
            {var subQ0=sQuery(id+"F0.wireOp",EDGE,"E37.0.3.0");var subQ1=sQuery(id+"F0.wireOp",EDGE,"E15.8");var subQ2=makeQuery(id+"F0.imprint","INTERSECT",VERTEX,{"derivedFrom":[subQ1,subQ0]});Q4=makeQuery(id+"F0.imprint","IMPRINT",FACE,{"disambiguationData":[TD([[makeQuery(id+"F0.imprint","IMPRINT",EDGE,{"disambiguationData":[TD([[subQ2,-1.0]])],"derivedFrom":subQ1}),-1.0]])]});}
            var Q5;
            {var subQ0=sQuery(id+"F0.wireOp",EDGE,"E37.0.4.0");Q5=makeQuery(id+"F0.imprint","IMPRINT",FACE,{"disambiguationData":[TD([[makeQuery(id+"F0.imprint","IMPRINT",EDGE,{"derivedFrom":subQ0}),1.0]])]});}
            var Q6;
            {var subQ0=sQuery(id+"F0.wireOp",EDGE,"E37.0.4.0");Q6=makeQuery(id+"F0.imprint","IMPRINT",FACE,{"disambiguationData":[TD([[makeQuery(id+"F0.imprint","IMPRINT",EDGE,{"derivedFrom":subQ0}),-1.0]])]});}
            var Q7;
            {var subQ0=sQuery(id+"F0.wireOp",EDGE,"E37.0.6.0");var subQ1=sQuery(id+"F0.wireOp",EDGE,"E15.8");var subQ2=makeQuery(id+"F0.imprint","INTERSECT",VERTEX,{"derivedFrom":[subQ1,subQ0]});Q7=makeQuery(id+"F0.imprint","IMPRINT",FACE,{"disambiguationData":[TD([[makeQuery(id+"F0.imprint","IMPRINT",EDGE,{"disambiguationData":[TD([[subQ2,-1.0]])],"derivedFrom":subQ1}),-1.0]])]});}
            var Q8;
            {var subQ0=sQuery(id+"F0.wireOp",EDGE,"E37.0.7.0");var subQ1=sQuery(id+"F0.wireOp",EDGE,"E15.8");var subQ2=makeQuery(id+"F0.imprint","INTERSECT",VERTEX,{"derivedFrom":[subQ1,subQ0]});Q8=makeQuery(id+"F0.imprint","IMPRINT",FACE,{"disambiguationData":[TD([[makeQuery(id+"F0.imprint","IMPRINT",EDGE,{"disambiguationData":[TD([[subQ2,-1.0]])],"derivedFrom":subQ1}),-1.0]])]});}
            var Q9;
            {var subQ0=sQuery(id+"F0.wireOp",EDGE,"E37.0.8.0");var subQ1=sQuery(id+"F0.wireOp",EDGE,"E15.8");var subQ2=makeQuery(id+"F0.imprint","INTERSECT",VERTEX,{"derivedFrom":[subQ1,subQ0]});Q9=makeQuery(id+"F0.imprint","IMPRINT",FACE,{"disambiguationData":[TD([[makeQuery(id+"F0.imprint","IMPRINT",EDGE,{"disambiguationData":[TD([[subQ2,-1.0]])],"derivedFrom":subQ1}),-1.0]])]});}
            var Q10;
            {var subQ3=sQuery(id+"F0.wireOp",EDGE,"E15.8");var subQ7=sQuery(id+"F0.wireOp",EDGE,"E15.7");var subQ8=makeQuery(id+"F0.imprint","INTERSECT",VERTEX,{"derivedFrom":[subQ7,subQ3]});Q10=makeQuery(id+"F0.imprint","IMPRINT",FACE,{"disambiguationData":[TD([[makeQuery(id+"F0.imprint","IMPRINT",EDGE,{"disambiguationData":[TD([[subQ8,1.0]])],"derivedFrom":subQ7}),-1.0]])]});}
            var Q11;
            {var subQ3=sQuery(id+"F0.wireOp",EDGE,"E15.7");var subQ7=sQuery(id+"F0.wireOp",EDGE,"E15.6");var subQ8=makeQuery(id+"F0.imprint","INTERSECT",VERTEX,{"derivedFrom":[subQ7,subQ3]});Q11=makeQuery(id+"F0.imprint","IMPRINT",FACE,{"disambiguationData":[TD([[makeQuery(id+"F0.imprint","IMPRINT",EDGE,{"disambiguationData":[TD([[subQ8,1.0]])],"derivedFrom":subQ7}),-1.0]])]});}
            var Q12;
            {var subQ0=sQuery(id+"F0.wireOp",EDGE,"E37.0.11.0");var subQ1=sQuery(id+"F0.wireOp",EDGE,"E15.6");var subQ2=makeQuery(id+"F0.imprint","INTERSECT",VERTEX,{"derivedFrom":[subQ1,subQ0]});Q12=makeQuery(id+"F0.imprint","IMPRINT",FACE,{"disambiguationData":[TD([[makeQuery(id+"F0.imprint","IMPRINT",EDGE,{"disambiguationData":[TD([[subQ2,-1.0]])],"derivedFrom":subQ1}),-1.0]])]});}
            var Q13;
            {var subQ0=sQuery(id+"F0.wireOp",EDGE,"E37.0.12.0");var subQ1=sQuery(id+"F0.wireOp",EDGE,"E15.6");var subQ2=makeQuery(id+"F0.imprint","INTERSECT",VERTEX,{"derivedFrom":[subQ1,subQ0]});Q13=makeQuery(id+"F0.imprint","IMPRINT",FACE,{"disambiguationData":[TD([[makeQuery(id+"F0.imprint","IMPRINT",EDGE,{"disambiguationData":[TD([[subQ2,-1.0]])],"derivedFrom":subQ1}),-1.0]])]});}
            var Q14;
            {var subQ0=sQuery(id+"F0.wireOp",EDGE,"E42.0.0.13");var subQ1=sQuery(id+"F0.wireOp",EDGE,"E15.6");var subQ2=makeQuery(id+"F0.imprint","INTERSECT",VERTEX,{"derivedFrom":[subQ1,subQ0]});Q14=makeQuery(id+"F0.imprint","IMPRINT",FACE,{"disambiguationData":[TD([[makeQuery(id+"F0.imprint","IMPRINT",EDGE,{"disambiguationData":[TD([[subQ2,-1.0]])],"derivedFrom":subQ1}),-1.0]])]});}
            var Q15;
            {var subQ0=sQuery(id+"F0.wireOp",EDGE,"E21");var subQ1=sQuery(id+"F0.wireOp",EDGE,"E17");var subQ2=makeQuery(id+"F0.imprint","INTERSECT",VERTEX,{"derivedFrom":[subQ1,subQ0]});Q15=makeQuery(id+"F0.imprint","IMPRINT",FACE,{"disambiguationData":[TD([[makeQuery(id+"F0.imprint","IMPRINT",EDGE,{"disambiguationData":[TD([[subQ2,1.0]])],"derivedFrom":subQ1}),1.0]])]});}
            var Q16;
            {var subQ0=sQuery(id+"F0.wireOp",EDGE,"E22");Q16=makeQuery(id+"F0.imprint","IMPRINT",FACE,{"disambiguationData":[TD([[makeQuery(id+"F0.imprint","IMPRINT",EDGE,{"derivedFrom":subQ0}),1.0]])]});}
            extrude(context, id + "F5", {"entities" : qUnion([Q0, Q1, Q2, Q3, Q4, Q5, Q6, Q7, Q8, Q9, Q10, Q11, Q12, Q13, Q14, Q15, Q16]), "depth" : 78 * mm, "offsetDistance" : 25 * mm});
        }
        {
            var Q0;
            {var subQ0=sQuery(id+"F0.wireOp",EDGE,"E37.0.6.0");Q0=makeQuery(id+"F0.imprint","IMPRINT",FACE,{"disambiguationData":[TD([[makeQuery(id+"F0.imprint","IMPRINT",EDGE,{"derivedFrom":subQ0}),-1.0]])]});}
            var Q1;
            {var subQ0=sQuery(id+"F0.wireOp",EDGE,"E37.0.4.0");Q1=makeQuery(id+"F0.imprint","IMPRINT",FACE,{"disambiguationData":[TD([[makeQuery(id+"F0.imprint","IMPRINT",EDGE,{"derivedFrom":subQ0}),-1.0]])]});}
            var Q2;
            {var subQ0=sQuery(id+"F0.wireOp",EDGE,"E37.0.2.0");Q2=makeQuery(id+"F0.imprint","IMPRINT",FACE,{"disambiguationData":[TD([[makeQuery(id+"F0.imprint","IMPRINT",EDGE,{"derivedFrom":subQ0}),-1.0]])]});}
            var Q3;
            {var subQ0=sQuery(id+"F0.wireOp",EDGE,"E36");Q3=makeQuery(id+"F0.imprint","IMPRINT",FACE,{"disambiguationData":[TD([[makeQuery(id+"F0.imprint","IMPRINT",EDGE,{"derivedFrom":subQ0}),-1.0]])]});}
            var Q4;
            {var subQ0=sQuery(id+"F0.wireOp",EDGE,"E30");Q4=makeQuery(id+"F0.imprint","IMPRINT",FACE,{"disambiguationData":[TD([[makeQuery(id+"F0.imprint","IMPRINT",EDGE,{"derivedFrom":subQ0}),1.0]])]});}
            var Q5;
            {var subQ0=sQuery(id+"F0.wireOp",EDGE,"E18");Q5=makeQuery(id+"F0.imprint","IMPRINT",FACE,{"disambiguationData":[TD([[makeQuery(id+"F0.imprint","IMPRINT",EDGE,{"derivedFrom":subQ0}),-1.0]])]});}
            var Q6;
            {var subQ0=sQuery(id+"F0.wireOp",EDGE,"E28.0.1.0");Q6=makeQuery(id+"F0.imprint","IMPRINT",FACE,{"disambiguationData":[TD([[makeQuery(id+"F0.imprint","IMPRINT",EDGE,{"derivedFrom":subQ0}),-1.0]])]});}
            var Q7;
            {var subQ0=sQuery(id+"F0.wireOp",EDGE,"E28.0.3.0");Q7=makeQuery(id+"F0.imprint","IMPRINT",FACE,{"disambiguationData":[TD([[makeQuery(id+"F0.imprint","IMPRINT",EDGE,{"derivedFrom":subQ0}),-1.0]])]});}
            var Q8;
            {var subQ0=sQuery(id+"F0.wireOp",EDGE,"E28.0.5.0");Q8=makeQuery(id+"F0.imprint","IMPRINT",FACE,{"disambiguationData":[TD([[makeQuery(id+"F0.imprint","IMPRINT",EDGE,{"derivedFrom":subQ0}),-1.0]])]});}
            var Q9;
            {var subQ0=sQuery(id+"F0.wireOp",EDGE,"E28.0.7.0");Q9=makeQuery(id+"F0.imprint","IMPRINT",FACE,{"disambiguationData":[TD([[makeQuery(id+"F0.imprint","IMPRINT",EDGE,{"derivedFrom":subQ0}),-1.0]])]});}
            var Q10;
            {var subQ0=sQuery(id+"F0.wireOp",EDGE,"E28.0.9.0");Q10=makeQuery(id+"F0.imprint","IMPRINT",FACE,{"disambiguationData":[TD([[makeQuery(id+"F0.imprint","IMPRINT",EDGE,{"derivedFrom":subQ0}),-1.0]])]});}
            var Q11;
            {var subQ0=sQuery(id+"F0.wireOp",EDGE,"E28.0.11.0");Q11=makeQuery(id+"F0.imprint","IMPRINT",FACE,{"disambiguationData":[TD([[makeQuery(id+"F0.imprint","IMPRINT",EDGE,{"derivedFrom":subQ0}),-1.0]])]});}
            var Q12;
            {var subQ0=sQuery(id+"F0.wireOp",EDGE,"E28.0.13.0");Q12=makeQuery(id+"F0.imprint","IMPRINT",FACE,{"disambiguationData":[TD([[makeQuery(id+"F0.imprint","IMPRINT",EDGE,{"derivedFrom":subQ0}),-1.0]])]});}
            var Q13;
            {var subQ0=sQuery(id+"F0.wireOp",EDGE,"E28.0.15.0");Q13=makeQuery(id+"F0.imprint","IMPRINT",FACE,{"disambiguationData":[TD([[makeQuery(id+"F0.imprint","IMPRINT",EDGE,{"derivedFrom":subQ0}),-1.0]])]});}
            var Q14;
            {var subQ0=sQuery(id+"F0.wireOp",EDGE,"E28.0.17.0");Q14=makeQuery(id+"F0.imprint","IMPRINT",FACE,{"disambiguationData":[TD([[makeQuery(id+"F0.imprint","IMPRINT",EDGE,{"derivedFrom":subQ0}),-1.0]])]});}
            var Q15;
            Q15=makeQuery(id+"F0.imprint","IMPRINT",FACE,{"disambiguationData":[TD([[makeQuery(id+"F0.imprint","IMPRINT",EDGE,{"derivedFrom":sQuery(id+"F0.wireOp",EDGE,"E15.0")}),1.0]])]});
            var Q16;
            {var subQ0=sQuery(id+"F0.wireOp",EDGE,"E20");Q16=makeQuery(id+"F0.imprint","IMPRINT",FACE,{"disambiguationData":[TD([[makeQuery(id+"F0.imprint","IMPRINT",EDGE,{"derivedFrom":subQ0}),-1.0]])]});}
            var Q17;
            {var subQ4=sQuery(id+"F0.wireOp",EDGE,"E19");Q17=makeQuery(id+"F0.imprint","IMPRINT",FACE,{"disambiguationData":[TD([[makeQuery(id+"F0.imprint","IMPRINT",EDGE,{"derivedFrom":subQ4}),-1.0]])]});}
            var Q18;
            Q18=makeQuery(id+"F0.imprint","IMPRINT",FACE,{"disambiguationData":[TD([[makeQuery(id+"F0.imprint","IMPRINT",EDGE,{"derivedFrom":sQuery(id+"F0.wireOp",EDGE,"E23")}),1.0]])]});
            var Q19;
            Q19=makeQuery(id+"F0.imprint","IMPRINT",FACE,{"disambiguationData":[TD([[makeQuery(id+"F0.imprint","IMPRINT",EDGE,{"derivedFrom":sQuery(id+"F0.wireOp",EDGE,"E24")}),1.0]])]});
            var Q20;
            {var subQ4=sQuery(id+"F0.wireOp",EDGE,"E18");Q20=makeQuery(id+"F0.imprint","IMPRINT",FACE,{"disambiguationData":[TD([[makeQuery(id+"F0.imprint","IMPRINT",EDGE,{"derivedFrom":subQ4}),1.0]])]});}
            var Q21;
            {var subQ2=sQuery(id+"F0.wireOp",EDGE,"E16");Q21=makeQuery(id+"F0.imprint","IMPRINT",FACE,{"disambiguationData":[TD([[makeQuery(id+"F0.imprint","IMPRINT",EDGE,{"derivedFrom":subQ2}),1.0]])]});}
            var Q22;
            {var subQ0=sQuery(id+"F0.wireOp",EDGE,"E32");Q22=makeQuery(id+"F0.imprint","IMPRINT",FACE,{"disambiguationData":[TD([[makeQuery(id+"F0.imprint","IMPRINT",EDGE,{"derivedFrom":subQ0}),-1.0]])]});}
            var Q23;
            {var subQ3=sQuery(id+"F0.wireOp",EDGE,"E37.0.8.0");Q23=makeQuery(id+"F0.imprint","IMPRINT",FACE,{"disambiguationData":[TD([[makeQuery(id+"F0.imprint","IMPRINT",EDGE,{"derivedFrom":subQ3}),-1.0]])]});}
            var Q24;
            {var subQ0=sQuery(id+"F0.wireOp",EDGE,"E37.0.10.0");Q24=makeQuery(id+"F0.imprint","IMPRINT",FACE,{"disambiguationData":[TD([[makeQuery(id+"F0.imprint","IMPRINT",EDGE,{"derivedFrom":subQ0}),-1.0]])]});}
            var Q25;
            {var subQ0=sQuery(id+"F0.wireOp",EDGE,"E37.0.12.0");Q25=makeQuery(id+"F0.imprint","IMPRINT",FACE,{"disambiguationData":[TD([[makeQuery(id+"F0.imprint","IMPRINT",EDGE,{"derivedFrom":subQ0}),-1.0]])]});}
            var Q26;
            {var subQ2=sQuery(id+"F0.wireOp",EDGE,"E17");Q26=makeQuery(id+"F0.imprint","IMPRINT",FACE,{"disambiguationData":[TD([[makeQuery(id+"F0.imprint","IMPRINT",EDGE,{"derivedFrom":subQ2}),-1.0]])]});}
            var Q27;
            {var subQ0=sQuery(id+"F0.wireOp",EDGE,"E29");Q27=makeQuery(id+"F0.imprint","IMPRINT",FACE,{"disambiguationData":[TD([[makeQuery(id+"F0.imprint","IMPRINT",EDGE,{"derivedFrom":subQ0}),-1.0]])]});}
            var Q28;
            {var subQ3=sQuery(id+"F0.wireOp",EDGE,"E60");Q28=makeQuery(id+"F0.imprint","IMPRINT",FACE,{"disambiguationData":[TD([[makeQuery(id+"F0.imprint","IMPRINT",EDGE,{"derivedFrom":subQ3}),-1.0]])]});}
            var Q29;
            {var subQ5=sQuery(id+"F0.wireOp",EDGE,"E11");var subQ6=sQuery(id+"F0.wireOp",EDGE,"E8");var subQ7=makeQuery(id+"F0.imprint","INTERSECT",VERTEX,{"derivedFrom":[subQ6,subQ5]});Q29=makeQuery(id+"F0.imprint","IMPRINT",FACE,{"disambiguationData":[TD([[makeQuery(id+"F0.imprint","IMPRINT",EDGE,{"disambiguationData":[TD([[subQ7,-1.0]])],"derivedFrom":subQ6}),-1.0]])]});}
            var Q30;
            {var subQ0=sQuery(id+"F0.wireOp",EDGE,"E63");Q30=makeQuery(id+"F0.imprint","IMPRINT",FACE,{"disambiguationData":[TD([[makeQuery(id+"F0.imprint","IMPRINT",EDGE,{"derivedFrom":subQ0}),1.0]])]});}
            var Q31;
            {var subQ0=sQuery(id+"F0.wireOp",EDGE,"E61");Q31=makeQuery(id+"F0.imprint","IMPRINT",FACE,{"disambiguationData":[TD([[makeQuery(id+"F0.imprint","IMPRINT",EDGE,{"derivedFrom":subQ0}),1.0]])]});}
            var Q32;
            {var subQ0=sQuery(id+"F0.wireOp",EDGE,"E65");Q32=makeQuery(id+"F0.imprint","IMPRINT",FACE,{"disambiguationData":[TD([[makeQuery(id+"F0.imprint","IMPRINT",EDGE,{"derivedFrom":subQ0}),1.0]])]});}
            var Q33;
            {var subQ0=sQuery(id+"F0.wireOp",EDGE,"E35");Q33=makeQuery(id+"F0.imprint","IMPRINT",FACE,{"disambiguationData":[TD([[makeQuery(id+"F0.imprint","IMPRINT",EDGE,{"derivedFrom":subQ0}),-1.0]])]});}
            var Q34;
            Q34=makeQuery(id+"F0.imprint","IMPRINT",FACE,{"disambiguationData":[TD([[makeQuery(id+"F0.imprint","IMPRINT",EDGE,{"derivedFrom":sQuery(id+"F0.wireOp",EDGE,"Vw2FYUNY-sn0W-j9As-YmBz-oMZoDKJWB2aW.bottom")}),1.0]])]});
            extrude(context, id + "F6", {"entities" : qUnion([Q0, Q1, Q2, Q3, Q4, Q5, Q6, Q7, Q8, Q9, Q10, Q11, Q12, Q13, Q14, Q15, Q16, Q17, Q18, Q19, Q20, Q21, Q22, Q23, Q24, Q25, Q26, Q27, Q28, Q29, Q30, Q31, Q32, Q33, Q34]), "depth" : 78 * mm, "offsetDistance" : 25 * mm, "hasSecondDirection" : true, "secondDirectionOppositeDirection" : false, "secondDirectionDepth" : 74 * mm});
        }
        {
            var Q0;
            Q0=makeQuery(id+"F5.opExtrude","SWEPT_FACE",FACE,{"disambiguationData":[OSD([sQuery(id+"F0.wireOp",EDGE,"E15.2"),sQuery(id+"F0.wireOp",EDGE,"E15.6"),sQuery(id+"F0.wireOp",EDGE,"E15.7"),sQuery(id+"F0.wireOp",EDGE,"E15.8"),sQuery(id+"F0.wireOp",EDGE,"E15.9")])]});
            var sketch = newSketch(context, id + "F7", { "sketchPlane" : qUnion([Q0])});
            skLineSegment(sketch, "E74", {"start": v(10.5, 151.48) * mm, "end": v(67.5, 151.48) * mm});
            skLineSegment(sketch, "E75", {"start": v(67.5, 151.48) * mm, "end": v(67.5, 65.47) * mm});
            skLineSegment(sketch, "E76", {"start": v(67.5, 65.47) * mm, "end": v(10.5, 65.47) * mm});
            skLineSegment(sketch, "E77", {"start": v(10.5, 65.47) * mm, "end": v(10.5, 151.48) * mm});
            skLineSegment(sketch, "E78", {"start": v(10.5, 151.48) * mm, "end": v(0, 151.48) * mm, "construction": true});
            skLineSegment(sketch, "E79", {"start": v(67.5, 151.48) * mm, "end": v(78, 151.48) * mm, "construction": true});
            skLineSegment(sketch, "E80.bottom", {"start": v(12, 149.98) * mm, "end": v(66, 149.98) * mm});
            skLineSegment(sketch, "E80.top", {"start": v(12, 69.97) * mm, "end": v(66, 69.97) * mm});
            skLineSegment(sketch, "E80.left", {"start": v(12, 149.98) * mm, "end": v(12, 69.97) * mm});
            skLineSegment(sketch, "E80.right", {"start": v(66, 149.98) * mm, "end": v(66, 69.97) * mm});
            skLineSegment(sketch, "E81.bottom", {"start": v(9.05, 55.47) * mm, "end": v(68.95, 55.47) * mm});
            skLineSegment(sketch, "E81.top", {"start": v(9.05, 16.08) * mm, "end": v(68.95, 16.08) * mm});
            skLineSegment(sketch, "E81.left", {"start": v(9.05, 55.47) * mm, "end": v(9.05, 16.08) * mm});
            skLineSegment(sketch, "E81.right", {"start": v(68.95, 55.47) * mm, "end": v(68.95, 16.08) * mm});
            skLineSegment(sketch, "E82", {"start": v(9.05, 55.47) * mm, "end": v(0, 55.47) * mm, "construction": true});
            skLineSegment(sketch, "E83", {"start": v(68.95, 55.47) * mm, "end": v(78, 55.47) * mm, "construction": true});
            skSolve(sketch);
        }
        {
            var Q0;
            Q0=makeQuery(id+"F7.imprint","IMPRINT",FACE,{"disambiguationData":[TD([[makeQuery(id+"F7.imprint","IMPRINT",EDGE,{"derivedFrom":sQuery(id+"F7.wireOp",EDGE,"E74")}),-1.0]])]});
            var Q1;
            Q1=makeQuery(id+"F7.imprint","IMPRINT",FACE,{"disambiguationData":[TD([[makeQuery(id+"F7.imprint","IMPRINT",EDGE,{"derivedFrom":sQuery(id+"F7.wireOp",EDGE,"E80.bottom")}),-1.0]])]});
            var Q2;
            Q2=makeQuery(id+"F7.imprint","IMPRINT",FACE,{"disambiguationData":[TD([[makeQuery(id+"F7.imprint","IMPRINT",EDGE,{"derivedFrom":sQuery(id+"F7.wireOp",EDGE,"E81.bottom")}),-1.0]])]});
            extrude(context, id + "F8", {"entities" : qUnion([Q0, Q1, Q2]), "operationType" : NewBodyOperationType.REMOVE, "oppositeDirection" : true, "depth" : 4 * mm, "offsetDistance" : 25 * mm});
        }
        {
            var Q0;
            Q0=makeQuery(id+"F7.imprint","IMPRINT",FACE,{"disambiguationData":[TD([[makeQuery(id+"F7.imprint","IMPRINT",EDGE,{"derivedFrom":sQuery(id+"F7.wireOp",EDGE,"E80.bottom")}),-1.0]])]});
            extrude(context, id + "F9", {"entities" : qUnion([Q0]), "operationType" : NewBodyOperationType.REMOVE, "oppositeDirection" : true, "depth" : -3 * mm, "offsetDistance" : 25 * mm});
        }
        {
            var Q0;
            Q0=makeQuery(id+"F1.opExtrude","SWEPT_BODY",BODY,{"disambiguationData":[OSD([sQuery(id+"F0.wireOp",EDGE,"E0"),sQuery(id+"F0.wireOp",EDGE,"E1"),sQuery(id+"F0.wireOp",EDGE,"E2"),sQuery(id+"F0.wireOp",EDGE,"E3"),sQuery(id+"F0.wireOp",EDGE,"E4"),sQuery(id+"F0.wireOp",EDGE,"E5"),sQuery(id+"F0.wireOp",EDGE,"E6"),sQuery(id+"F0.wireOp",EDGE,"E7"),sQuery(id+"F0.wireOp",EDGE,"E8"),sQuery(id+"F0.wireOp",EDGE,"E9.filletArc"),sQuery(id+"F0.wireOp",EDGE,"E10.filletArc"),sQuery(id+"F0.wireOp",EDGE,"E11"),sQuery(id+"F0.wireOp",EDGE,"E12"),sQuery(id+"F0.wireOp",EDGE,"E13.filletArc"),sQuery(id+"F0.wireOp",EDGE,"E14.filletArc"),sQuery(id+"F0.wireOp",EDGE,"E15.3"),sQuery(id+"F0.wireOp",EDGE,"E19"),sQuery(id+"F0.wireOp",EDGE,"E23"),sQuery(id+"F0.wireOp",EDGE,"E24"),sQuery(id+"F0.wireOp",EDGE,"E25"),sQuery(id+"F0.wireOp",EDGE,"E26"),sQuery(id+"F0.wireOp",EDGE,"E27"),sQuery(id+"F0.wireOp",EDGE,"E28.0.1.0"),sQuery(id+"F0.wireOp",EDGE,"E28.0.2.0"),sQuery(id+"F0.wireOp",EDGE,"E28.0.3.0"),sQuery(id+"F0.wireOp",EDGE,"E28.0.4.0"),sQuery(id+"F0.wireOp",EDGE,"E28.0.5.0"),sQuery(id+"F0.wireOp",EDGE,"E28.0.6.0"),sQuery(id+"F0.wireOp",EDGE,"E28.0.7.0"),sQuery(id+"F0.wireOp",EDGE,"E28.0.8.0"),sQuery(id+"F0.wireOp",EDGE,"E28.0.9.0"),sQuery(id+"F0.wireOp",EDGE,"E28.0.10.0"),sQuery(id+"F0.wireOp",EDGE,"E28.0.11.0"),sQuery(id+"F0.wireOp",EDGE,"E28.0.12.0"),sQuery(id+"F0.wireOp",EDGE,"E28.0.13.0"),sQuery(id+"F0.wireOp",EDGE,"E28.0.14.0"),sQuery(id+"F0.wireOp",EDGE,"E28.0.15.0"),sQuery(id+"F0.wireOp",EDGE,"E28.0.16.0"),sQuery(id+"F0.wireOp",EDGE,"E28.0.17.0"),sQuery(id+"F0.wireOp",EDGE,"E28.0.18.0")])]});
            var Q1;
            Q1=makeQuery(id+"F6.opExtrude","SWEPT_BODY",BODY,{"disambiguationData":[OSD([sQuery(id+"F0.wireOp",EDGE,"E0"),sQuery(id+"F0.wireOp",EDGE,"E1"),sQuery(id+"F0.wireOp",EDGE,"E2"),sQuery(id+"F0.wireOp",EDGE,"E3"),sQuery(id+"F0.wireOp",EDGE,"E7"),sQuery(id+"F0.wireOp",EDGE,"E8"),sQuery(id+"F0.wireOp",EDGE,"E9.filletArc"),sQuery(id+"F0.wireOp",EDGE,"E10.filletArc"),sQuery(id+"F0.wireOp",EDGE,"E11"),sQuery(id+"F0.wireOp",EDGE,"E12"),sQuery(id+"F0.wireOp",EDGE,"E15.3"),sQuery(id+"F0.wireOp",EDGE,"E19"),sQuery(id+"F0.wireOp",EDGE,"E27"),sQuery(id+"F0.wireOp",EDGE,"E28.0.1.0"),sQuery(id+"F0.wireOp",EDGE,"E28.0.2.0"),sQuery(id+"F0.wireOp",EDGE,"E28.0.3.0"),sQuery(id+"F0.wireOp",EDGE,"E28.0.4.0"),sQuery(id+"F0.wireOp",EDGE,"E28.0.5.0"),sQuery(id+"F0.wireOp",EDGE,"E28.0.6.0"),sQuery(id+"F0.wireOp",EDGE,"E28.0.7.0"),sQuery(id+"F0.wireOp",EDGE,"E28.0.8.0"),sQuery(id+"F0.wireOp",EDGE,"E28.0.9.0"),sQuery(id+"F0.wireOp",EDGE,"E28.0.10.0"),sQuery(id+"F0.wireOp",EDGE,"E28.0.11.0"),sQuery(id+"F0.wireOp",EDGE,"E28.0.12.0"),sQuery(id+"F0.wireOp",EDGE,"E28.0.13.0"),sQuery(id+"F0.wireOp",EDGE,"E28.0.14.0"),sQuery(id+"F0.wireOp",EDGE,"E28.0.15.0"),sQuery(id+"F0.wireOp",EDGE,"E28.0.16.0"),sQuery(id+"F0.wireOp",EDGE,"E28.0.17.0"),sQuery(id+"F0.wireOp",EDGE,"E28.0.18.0")])]});
            var Q2;
            Q2=makeQuery(id+"F2.opExtrude","SWEPT_BODY",BODY,{"disambiguationData":[OSD([sQuery(id+"F0.wireOp",EDGE,"E3"),sQuery(id+"F0.wireOp",EDGE,"E15.3"),sQuery(id+"F0.wireOp",EDGE,"E18"),sQuery(id+"F0.wireOp",EDGE,"E19")])]});
            booleanBodies(context, id + "F10", {"operationType" : BooleanOperationType.SUBTRACTION, "tools" : qUnion([Q0, Q1]), "targets" : qUnion([Q2]), "keepTools" : true});
        }
        {
            var Q0;
            Q0=makeQuery(id+"F6.opExtrude","SWEPT_BODY",BODY,{"disambiguationData":[OSD([sQuery(id+"F0.wireOp",EDGE,"E0"),sQuery(id+"F0.wireOp",EDGE,"E1"),sQuery(id+"F0.wireOp",EDGE,"E2"),sQuery(id+"F0.wireOp",EDGE,"E3"),sQuery(id+"F0.wireOp",EDGE,"E7"),sQuery(id+"F0.wireOp",EDGE,"E8"),sQuery(id+"F0.wireOp",EDGE,"E10.filletArc"),sQuery(id+"F0.wireOp",EDGE,"E11"),sQuery(id+"F0.wireOp",EDGE,"E12"),sQuery(id+"F0.wireOp",EDGE,"E15.3"),sQuery(id+"F0.wireOp",EDGE,"E15.4"),sQuery(id+"F0.wireOp",EDGE,"E15.5"),sQuery(id+"F0.wireOp",EDGE,"E15.9"),sQuery(id+"F0.wireOp",EDGE,"E16"),sQuery(id+"F0.wireOp",EDGE,"E19"),sQuery(id+"F0.wireOp",EDGE,"E27"),sQuery(id+"F0.wireOp",EDGE,"E28.0.1.0"),sQuery(id+"F0.wireOp",EDGE,"E28.0.2.0"),sQuery(id+"F0.wireOp",EDGE,"E28.0.3.0"),sQuery(id+"F0.wireOp",EDGE,"E28.0.4.0"),sQuery(id+"F0.wireOp",EDGE,"E28.0.5.0"),sQuery(id+"F0.wireOp",EDGE,"E28.0.6.0"),sQuery(id+"F0.wireOp",EDGE,"E28.0.7.0"),sQuery(id+"F0.wireOp",EDGE,"E28.0.8.0"),sQuery(id+"F0.wireOp",EDGE,"E28.0.9.0"),sQuery(id+"F0.wireOp",EDGE,"E28.0.10.0"),sQuery(id+"F0.wireOp",EDGE,"E28.0.11.0"),sQuery(id+"F0.wireOp",EDGE,"E28.0.12.0"),sQuery(id+"F0.wireOp",EDGE,"E28.0.13.0"),sQuery(id+"F0.wireOp",EDGE,"E28.0.14.0"),sQuery(id+"F0.wireOp",EDGE,"E28.0.15.0"),sQuery(id+"F0.wireOp",EDGE,"E28.0.16.0"),sQuery(id+"F0.wireOp",EDGE,"E28.0.17.0"),sQuery(id+"F0.wireOp",EDGE,"E28.0.18.0"),sQuery(id+"F0.wireOp",EDGE,"E29"),sQuery(id+"F0.wireOp",EDGE,"E30"),sQuery(id+"F0.wireOp",EDGE,"E31"),sQuery(id+"F0.wireOp",EDGE,"E32"),sQuery(id+"F0.wireOp",EDGE,"E33")])]});
            var Q1;
            Q1=makeQuery(id+"F1.opExtrude","SWEPT_BODY",BODY,{"disambiguationData":[OSD([sQuery(id+"F0.wireOp",EDGE,"E0"),sQuery(id+"F0.wireOp",EDGE,"E1"),sQuery(id+"F0.wireOp",EDGE,"E2"),sQuery(id+"F0.wireOp",EDGE,"E3"),sQuery(id+"F0.wireOp",EDGE,"E4"),sQuery(id+"F0.wireOp",EDGE,"E5"),sQuery(id+"F0.wireOp",EDGE,"E6"),sQuery(id+"F0.wireOp",EDGE,"E7"),sQuery(id+"F0.wireOp",EDGE,"E8"),sQuery(id+"F0.wireOp",EDGE,"E10.filletArc"),sQuery(id+"F0.wireOp",EDGE,"E11"),sQuery(id+"F0.wireOp",EDGE,"E12"),sQuery(id+"F0.wireOp",EDGE,"E13.filletArc"),sQuery(id+"F0.wireOp",EDGE,"E14.filletArc"),sQuery(id+"F0.wireOp",EDGE,"E15.3"),sQuery(id+"F0.wireOp",EDGE,"E15.4"),sQuery(id+"F0.wireOp",EDGE,"E15.5"),sQuery(id+"F0.wireOp",EDGE,"E15.9"),sQuery(id+"F0.wireOp",EDGE,"E16"),sQuery(id+"F0.wireOp",EDGE,"E19"),sQuery(id+"F0.wireOp",EDGE,"E23"),sQuery(id+"F0.wireOp",EDGE,"E24"),sQuery(id+"F0.wireOp",EDGE,"E25"),sQuery(id+"F0.wireOp",EDGE,"E26"),sQuery(id+"F0.wireOp",EDGE,"E27"),sQuery(id+"F0.wireOp",EDGE,"E28.0.1.0"),sQuery(id+"F0.wireOp",EDGE,"E28.0.2.0"),sQuery(id+"F0.wireOp",EDGE,"E28.0.3.0"),sQuery(id+"F0.wireOp",EDGE,"E28.0.4.0"),sQuery(id+"F0.wireOp",EDGE,"E28.0.5.0"),sQuery(id+"F0.wireOp",EDGE,"E28.0.6.0"),sQuery(id+"F0.wireOp",EDGE,"E28.0.7.0"),sQuery(id+"F0.wireOp",EDGE,"E28.0.8.0"),sQuery(id+"F0.wireOp",EDGE,"E28.0.9.0"),sQuery(id+"F0.wireOp",EDGE,"E28.0.10.0"),sQuery(id+"F0.wireOp",EDGE,"E28.0.11.0"),sQuery(id+"F0.wireOp",EDGE,"E28.0.12.0"),sQuery(id+"F0.wireOp",EDGE,"E28.0.13.0"),sQuery(id+"F0.wireOp",EDGE,"E28.0.14.0"),sQuery(id+"F0.wireOp",EDGE,"E28.0.15.0"),sQuery(id+"F0.wireOp",EDGE,"E28.0.16.0"),sQuery(id+"F0.wireOp",EDGE,"E28.0.17.0"),sQuery(id+"F0.wireOp",EDGE,"E28.0.18.0"),sQuery(id+"F0.wireOp",EDGE,"E29"),sQuery(id+"F0.wireOp",EDGE,"E30"),sQuery(id+"F0.wireOp",EDGE,"E31"),sQuery(id+"F0.wireOp",EDGE,"E32"),sQuery(id+"F0.wireOp",EDGE,"E33")])]});
            var Q2;
            Q2=makeQuery(id+"F3.opExtrude","SWEPT_BODY",BODY,{"disambiguationData":[OSD([sQuery(id+"F0.wireOp",EDGE,"E2"),sQuery(id+"F0.wireOp",EDGE,"E3"),sQuery(id+"F0.wireOp",EDGE,"E7"),sQuery(id+"F0.wireOp",EDGE,"E9.filletArc"),sQuery(id+"F0.wireOp",EDGE,"E15.4"),sQuery(id+"F0.wireOp",EDGE,"E15.5"),sQuery(id+"F0.wireOp",EDGE,"E15.9"),sQuery(id+"F0.wireOp",EDGE,"E16"),sQuery(id+"F0.wireOp",EDGE,"E18")])]});
            booleanBodies(context, id + "F11", {"operationType" : BooleanOperationType.SUBTRACTION, "tools" : qUnion([Q0, Q1]), "targets" : qUnion([Q2]), "keepTools" : true});
        }
        {
            var Q0;
            Q0=makeQuery(id+"F1.opExtrude","SWEPT_BODY",BODY,{"disambiguationData":[OSD([sQuery(id+"F0.wireOp",EDGE,"E0"),sQuery(id+"F0.wireOp",EDGE,"E1"),sQuery(id+"F0.wireOp",EDGE,"E2"),sQuery(id+"F0.wireOp",EDGE,"E3"),sQuery(id+"F0.wireOp",EDGE,"E4"),sQuery(id+"F0.wireOp",EDGE,"E5"),sQuery(id+"F0.wireOp",EDGE,"E6"),sQuery(id+"F0.wireOp",EDGE,"E7"),sQuery(id+"F0.wireOp",EDGE,"E8"),sQuery(id+"F0.wireOp",EDGE,"E10.filletArc"),sQuery(id+"F0.wireOp",EDGE,"E11"),sQuery(id+"F0.wireOp",EDGE,"E12"),sQuery(id+"F0.wireOp",EDGE,"E13.filletArc"),sQuery(id+"F0.wireOp",EDGE,"E14.filletArc"),sQuery(id+"F0.wireOp",EDGE,"E15.2"),sQuery(id+"F0.wireOp",EDGE,"E15.3"),sQuery(id+"F0.wireOp",EDGE,"E15.4"),sQuery(id+"F0.wireOp",EDGE,"E15.5"),sQuery(id+"F0.wireOp",EDGE,"E15.6"),sQuery(id+"F0.wireOp",EDGE,"E15.7"),sQuery(id+"F0.wireOp",EDGE,"E15.8"),sQuery(id+"F0.wireOp",EDGE,"E15.9"),sQuery(id+"F0.wireOp",EDGE,"E16"),sQuery(id+"F0.wireOp",EDGE,"E17"),sQuery(id+"F0.wireOp",EDGE,"E19"),sQuery(id+"F0.wireOp",EDGE,"E23"),sQuery(id+"F0.wireOp",EDGE,"E24"),sQuery(id+"F0.wireOp",EDGE,"E25"),sQuery(id+"F0.wireOp",EDGE,"E26"),sQuery(id+"F0.wireOp",EDGE,"E27"),sQuery(id+"F0.wireOp",EDGE,"E28.0.1.0"),sQuery(id+"F0.wireOp",EDGE,"E28.0.2.0"),sQuery(id+"F0.wireOp",EDGE,"E28.0.3.0"),sQuery(id+"F0.wireOp",EDGE,"E28.0.4.0"),sQuery(id+"F0.wireOp",EDGE,"E28.0.5.0"),sQuery(id+"F0.wireOp",EDGE,"E28.0.6.0"),sQuery(id+"F0.wireOp",EDGE,"E28.0.7.0"),sQuery(id+"F0.wireOp",EDGE,"E28.0.8.0"),sQuery(id+"F0.wireOp",EDGE,"E28.0.9.0"),sQuery(id+"F0.wireOp",EDGE,"E28.0.10.0"),sQuery(id+"F0.wireOp",EDGE,"E28.0.11.0"),sQuery(id+"F0.wireOp",EDGE,"E28.0.12.0"),sQuery(id+"F0.wireOp",EDGE,"E28.0.13.0"),sQuery(id+"F0.wireOp",EDGE,"E28.0.14.0"),sQuery(id+"F0.wireOp",EDGE,"E28.0.15.0"),sQuery(id+"F0.wireOp",EDGE,"E28.0.16.0"),sQuery(id+"F0.wireOp",EDGE,"E28.0.17.0"),sQuery(id+"F0.wireOp",EDGE,"E28.0.18.0"),sQuery(id+"F0.wireOp",EDGE,"E29"),sQuery(id+"F0.wireOp",EDGE,"E30"),sQuery(id+"F0.wireOp",EDGE,"E31"),sQuery(id+"F0.wireOp",EDGE,"E32"),sQuery(id+"F0.wireOp",EDGE,"E36"),sQuery(id+"F0.wireOp",EDGE,"E37.0.1.0"),sQuery(id+"F0.wireOp",EDGE,"E37.0.2.0"),sQuery(id+"F0.wireOp",EDGE,"E37.0.3.0"),sQuery(id+"F0.wireOp",EDGE,"E37.0.4.0"),sQuery(id+"F0.wireOp",EDGE,"E37.0.5.0"),sQuery(id+"F0.wireOp",EDGE,"E37.0.6.0"),sQuery(id+"F0.wireOp",EDGE,"E37.0.7.0"),sQuery(id+"F0.wireOp",EDGE,"E37.0.8.0"),sQuery(id+"F0.wireOp",EDGE,"E37.0.9.0"),sQuery(id+"F0.wireOp",EDGE,"E37.0.10.0"),sQuery(id+"F0.wireOp",EDGE,"E37.0.11.0"),sQuery(id+"F0.wireOp",EDGE,"E37.0.12.0"),sQuery(id+"F0.wireOp",EDGE,"E42.0.0.13")])]});
            var Q1;
            Q1=makeQuery(id+"F6.opExtrude","SWEPT_BODY",BODY,{"disambiguationData":[OSD([sQuery(id+"F0.wireOp",EDGE,"E0"),sQuery(id+"F0.wireOp",EDGE,"E1"),sQuery(id+"F0.wireOp",EDGE,"E2"),sQuery(id+"F0.wireOp",EDGE,"E3"),sQuery(id+"F0.wireOp",EDGE,"E7"),sQuery(id+"F0.wireOp",EDGE,"E8"),sQuery(id+"F0.wireOp",EDGE,"E10.filletArc"),sQuery(id+"F0.wireOp",EDGE,"E11"),sQuery(id+"F0.wireOp",EDGE,"E12"),sQuery(id+"F0.wireOp",EDGE,"E15.2"),sQuery(id+"F0.wireOp",EDGE,"E15.3"),sQuery(id+"F0.wireOp",EDGE,"E15.4"),sQuery(id+"F0.wireOp",EDGE,"E15.5"),sQuery(id+"F0.wireOp",EDGE,"E15.6"),sQuery(id+"F0.wireOp",EDGE,"E15.7"),sQuery(id+"F0.wireOp",EDGE,"E15.8"),sQuery(id+"F0.wireOp",EDGE,"E15.9"),sQuery(id+"F0.wireOp",EDGE,"E16"),sQuery(id+"F0.wireOp",EDGE,"E17"),sQuery(id+"F0.wireOp",EDGE,"E19"),sQuery(id+"F0.wireOp",EDGE,"E27"),sQuery(id+"F0.wireOp",EDGE,"E28.0.1.0"),sQuery(id+"F0.wireOp",EDGE,"E28.0.2.0"),sQuery(id+"F0.wireOp",EDGE,"E28.0.3.0"),sQuery(id+"F0.wireOp",EDGE,"E28.0.4.0"),sQuery(id+"F0.wireOp",EDGE,"E28.0.5.0"),sQuery(id+"F0.wireOp",EDGE,"E28.0.6.0"),sQuery(id+"F0.wireOp",EDGE,"E28.0.7.0"),sQuery(id+"F0.wireOp",EDGE,"E28.0.8.0"),sQuery(id+"F0.wireOp",EDGE,"E28.0.9.0"),sQuery(id+"F0.wireOp",EDGE,"E28.0.10.0"),sQuery(id+"F0.wireOp",EDGE,"E28.0.11.0"),sQuery(id+"F0.wireOp",EDGE,"E28.0.12.0"),sQuery(id+"F0.wireOp",EDGE,"E28.0.13.0"),sQuery(id+"F0.wireOp",EDGE,"E28.0.14.0"),sQuery(id+"F0.wireOp",EDGE,"E28.0.15.0"),sQuery(id+"F0.wireOp",EDGE,"E28.0.16.0"),sQuery(id+"F0.wireOp",EDGE,"E28.0.17.0"),sQuery(id+"F0.wireOp",EDGE,"E28.0.18.0"),sQuery(id+"F0.wireOp",EDGE,"E29"),sQuery(id+"F0.wireOp",EDGE,"E30"),sQuery(id+"F0.wireOp",EDGE,"E31"),sQuery(id+"F0.wireOp",EDGE,"E32"),sQuery(id+"F0.wireOp",EDGE,"E36"),sQuery(id+"F0.wireOp",EDGE,"E37.0.1.0"),sQuery(id+"F0.wireOp",EDGE,"E37.0.2.0"),sQuery(id+"F0.wireOp",EDGE,"E37.0.3.0"),sQuery(id+"F0.wireOp",EDGE,"E37.0.4.0"),sQuery(id+"F0.wireOp",EDGE,"E37.0.5.0"),sQuery(id+"F0.wireOp",EDGE,"E37.0.6.0"),sQuery(id+"F0.wireOp",EDGE,"E37.0.7.0"),sQuery(id+"F0.wireOp",EDGE,"E37.0.8.0"),sQuery(id+"F0.wireOp",EDGE,"E37.0.9.0"),sQuery(id+"F0.wireOp",EDGE,"E37.0.10.0"),sQuery(id+"F0.wireOp",EDGE,"E37.0.11.0"),sQuery(id+"F0.wireOp",EDGE,"E37.0.12.0"),sQuery(id+"F0.wireOp",EDGE,"E42.0.0.13")])]});
            var Q2;
            Q2=makeQuery(id+"F4.opExtrude","SWEPT_BODY",BODY,{"disambiguationData":[OSD([sQuery(id+"F0.wireOp",EDGE,"E1"),sQuery(id+"F0.wireOp",EDGE,"E7"),sQuery(id+"F0.wireOp",EDGE,"E8"),sQuery(id+"F0.wireOp",EDGE,"E11"),sQuery(id+"F0.wireOp",EDGE,"E12"),sQuery(id+"F0.wireOp",EDGE,"E15.2"),sQuery(id+"F0.wireOp",EDGE,"E15.6"),sQuery(id+"F0.wireOp",EDGE,"E15.7"),sQuery(id+"F0.wireOp",EDGE,"E15.8"),sQuery(id+"F0.wireOp",EDGE,"E15.9"),sQuery(id+"F0.wireOp",EDGE,"E16"),sQuery(id+"F0.wireOp",EDGE,"E17")])]});
            booleanBodies(context, id + "F12", {"operationType" : BooleanOperationType.SUBTRACTION, "tools" : qUnion([Q0, Q1]), "targets" : qUnion([Q2]), "keepTools" : true});
        }
        {
            var Q0;
            Q0=makeQuery(id+"F1.opExtrude","SWEPT_BODY",BODY,{"disambiguationData":[OSD([sQuery(id+"F0.wireOp",EDGE,"E0"),sQuery(id+"F0.wireOp",EDGE,"E1"),sQuery(id+"F0.wireOp",EDGE,"E2"),sQuery(id+"F0.wireOp",EDGE,"E3"),sQuery(id+"F0.wireOp",EDGE,"E4"),sQuery(id+"F0.wireOp",EDGE,"E5"),sQuery(id+"F0.wireOp",EDGE,"E6"),sQuery(id+"F0.wireOp",EDGE,"E7"),sQuery(id+"F0.wireOp",EDGE,"E8"),sQuery(id+"F0.wireOp",EDGE,"E10.filletArc"),sQuery(id+"F0.wireOp",EDGE,"E11"),sQuery(id+"F0.wireOp",EDGE,"E12"),sQuery(id+"F0.wireOp",EDGE,"E13.filletArc"),sQuery(id+"F0.wireOp",EDGE,"E14.filletArc"),sQuery(id+"F0.wireOp",EDGE,"E15.3"),sQuery(id+"F0.wireOp",EDGE,"E15.4"),sQuery(id+"F0.wireOp",EDGE,"E15.5"),sQuery(id+"F0.wireOp",EDGE,"E16"),sQuery(id+"F0.wireOp",EDGE,"E17"),sQuery(id+"F0.wireOp",EDGE,"E19"),sQuery(id+"F0.wireOp",EDGE,"E21"),sQuery(id+"F0.wireOp",EDGE,"E23"),sQuery(id+"F0.wireOp",EDGE,"E24"),sQuery(id+"F0.wireOp",EDGE,"E25"),sQuery(id+"F0.wireOp",EDGE,"E26"),sQuery(id+"F0.wireOp",EDGE,"E27"),sQuery(id+"F0.wireOp",EDGE,"E28.0.1.0"),sQuery(id+"F0.wireOp",EDGE,"E28.0.2.0"),sQuery(id+"F0.wireOp",EDGE,"E28.0.3.0"),sQuery(id+"F0.wireOp",EDGE,"E28.0.4.0"),sQuery(id+"F0.wireOp",EDGE,"E28.0.5.0"),sQuery(id+"F0.wireOp",EDGE,"E28.0.6.0"),sQuery(id+"F0.wireOp",EDGE,"E28.0.7.0"),sQuery(id+"F0.wireOp",EDGE,"E28.0.8.0"),sQuery(id+"F0.wireOp",EDGE,"E28.0.9.0"),sQuery(id+"F0.wireOp",EDGE,"E28.0.10.0"),sQuery(id+"F0.wireOp",EDGE,"E28.0.11.0"),sQuery(id+"F0.wireOp",EDGE,"E28.0.12.0"),sQuery(id+"F0.wireOp",EDGE,"E28.0.13.0"),sQuery(id+"F0.wireOp",EDGE,"E28.0.14.0"),sQuery(id+"F0.wireOp",EDGE,"E28.0.15.0"),sQuery(id+"F0.wireOp",EDGE,"E28.0.16.0"),sQuery(id+"F0.wireOp",EDGE,"E28.0.17.0"),sQuery(id+"F0.wireOp",EDGE,"E28.0.18.0"),sQuery(id+"F0.wireOp",EDGE,"E29"),sQuery(id+"F0.wireOp",EDGE,"E30"),sQuery(id+"F0.wireOp",EDGE,"E31"),sQuery(id+"F0.wireOp",EDGE,"E32"),sQuery(id+"F0.wireOp",EDGE,"E36"),sQuery(id+"F0.wireOp",EDGE,"E37.0.1.0"),sQuery(id+"F0.wireOp",EDGE,"E37.0.2.0"),sQuery(id+"F0.wireOp",EDGE,"E37.0.3.0"),sQuery(id+"F0.wireOp",EDGE,"E37.0.4.0"),sQuery(id+"F0.wireOp",EDGE,"E37.0.5.0"),sQuery(id+"F0.wireOp",EDGE,"E37.0.6.0"),sQuery(id+"F0.wireOp",EDGE,"E37.0.7.0"),sQuery(id+"F0.wireOp",EDGE,"E37.0.8.0"),sQuery(id+"F0.wireOp",EDGE,"E37.0.9.0"),sQuery(id+"F0.wireOp",EDGE,"E37.0.10.0"),sQuery(id+"F0.wireOp",EDGE,"E37.0.11.0"),sQuery(id+"F0.wireOp",EDGE,"E37.0.12.0"),sQuery(id+"F0.wireOp",EDGE,"E42.0.0.13"),sQuery(id+"F0.wireOp",EDGE,"E59"),sQuery(id+"F0.wireOp",EDGE,"E60")])]});
            var Q1;
            Q1=makeQuery(id+"F6.opExtrude","SWEPT_BODY",BODY,{"disambiguationData":[OSD([sQuery(id+"F0.wireOp",EDGE,"E0"),sQuery(id+"F0.wireOp",EDGE,"E1"),sQuery(id+"F0.wireOp",EDGE,"E2"),sQuery(id+"F0.wireOp",EDGE,"E3"),sQuery(id+"F0.wireOp",EDGE,"E7"),sQuery(id+"F0.wireOp",EDGE,"E8"),sQuery(id+"F0.wireOp",EDGE,"E10.filletArc"),sQuery(id+"F0.wireOp",EDGE,"E11"),sQuery(id+"F0.wireOp",EDGE,"E12"),sQuery(id+"F0.wireOp",EDGE,"E15.3"),sQuery(id+"F0.wireOp",EDGE,"E15.4"),sQuery(id+"F0.wireOp",EDGE,"E15.5"),sQuery(id+"F0.wireOp",EDGE,"E16"),sQuery(id+"F0.wireOp",EDGE,"E17"),sQuery(id+"F0.wireOp",EDGE,"E19"),sQuery(id+"F0.wireOp",EDGE,"E21"),sQuery(id+"F0.wireOp",EDGE,"E27"),sQuery(id+"F0.wireOp",EDGE,"E28.0.1.0"),sQuery(id+"F0.wireOp",EDGE,"E28.0.2.0"),sQuery(id+"F0.wireOp",EDGE,"E28.0.3.0"),sQuery(id+"F0.wireOp",EDGE,"E28.0.4.0"),sQuery(id+"F0.wireOp",EDGE,"E28.0.5.0"),sQuery(id+"F0.wireOp",EDGE,"E28.0.6.0"),sQuery(id+"F0.wireOp",EDGE,"E28.0.7.0"),sQuery(id+"F0.wireOp",EDGE,"E28.0.8.0"),sQuery(id+"F0.wireOp",EDGE,"E28.0.9.0"),sQuery(id+"F0.wireOp",EDGE,"E28.0.10.0"),sQuery(id+"F0.wireOp",EDGE,"E28.0.11.0"),sQuery(id+"F0.wireOp",EDGE,"E28.0.12.0"),sQuery(id+"F0.wireOp",EDGE,"E28.0.13.0"),sQuery(id+"F0.wireOp",EDGE,"E28.0.14.0"),sQuery(id+"F0.wireOp",EDGE,"E28.0.15.0"),sQuery(id+"F0.wireOp",EDGE,"E28.0.16.0"),sQuery(id+"F0.wireOp",EDGE,"E28.0.17.0"),sQuery(id+"F0.wireOp",EDGE,"E28.0.18.0"),sQuery(id+"F0.wireOp",EDGE,"E29"),sQuery(id+"F0.wireOp",EDGE,"E30"),sQuery(id+"F0.wireOp",EDGE,"E31"),sQuery(id+"F0.wireOp",EDGE,"E32"),sQuery(id+"F0.wireOp",EDGE,"E36"),sQuery(id+"F0.wireOp",EDGE,"E37.0.1.0"),sQuery(id+"F0.wireOp",EDGE,"E37.0.2.0"),sQuery(id+"F0.wireOp",EDGE,"E37.0.3.0"),sQuery(id+"F0.wireOp",EDGE,"E37.0.4.0"),sQuery(id+"F0.wireOp",EDGE,"E37.0.5.0"),sQuery(id+"F0.wireOp",EDGE,"E37.0.6.0"),sQuery(id+"F0.wireOp",EDGE,"E37.0.7.0"),sQuery(id+"F0.wireOp",EDGE,"E37.0.8.0"),sQuery(id+"F0.wireOp",EDGE,"E37.0.9.0"),sQuery(id+"F0.wireOp",EDGE,"E37.0.10.0"),sQuery(id+"F0.wireOp",EDGE,"E37.0.11.0"),sQuery(id+"F0.wireOp",EDGE,"E37.0.12.0"),sQuery(id+"F0.wireOp",EDGE,"E42.0.0.13"),sQuery(id+"F0.wireOp",EDGE,"E59"),sQuery(id+"F0.wireOp",EDGE,"E60")])]});
            var Q2;
            Q2=makeQuery(id+"F5.opExtrude","SWEPT_BODY",BODY,{"disambiguationData":[OSD([sQuery(id+"F0.wireOp",EDGE,"E15.2"),sQuery(id+"F0.wireOp",EDGE,"E15.6"),sQuery(id+"F0.wireOp",EDGE,"E15.7"),sQuery(id+"F0.wireOp",EDGE,"E15.8"),sQuery(id+"F0.wireOp",EDGE,"E15.9"),sQuery(id+"F0.wireOp",EDGE,"E20"),sQuery(id+"F0.wireOp",EDGE,"E21"),sQuery(id+"F0.wireOp",EDGE,"E22")])]});
            booleanBodies(context, id + "F13", {"operationType" : BooleanOperationType.SUBTRACTION, "tools" : qUnion([Q0, Q1]), "targets" : qUnion([Q2]), "keepTools" : true});
        }
        {
            var Q0;
            Q0=makeQuery(id+"F1.opExtrude","SWEPT_BODY",BODY,{"disambiguationData":[OSD([sQuery(id+"F0.wireOp",EDGE,"E0"),sQuery(id+"F0.wireOp",EDGE,"E1"),sQuery(id+"F0.wireOp",EDGE,"E2"),sQuery(id+"F0.wireOp",EDGE,"E3"),sQuery(id+"F0.wireOp",EDGE,"E4"),sQuery(id+"F0.wireOp",EDGE,"E5"),sQuery(id+"F0.wireOp",EDGE,"E6"),sQuery(id+"F0.wireOp",EDGE,"E7"),sQuery(id+"F0.wireOp",EDGE,"E8"),sQuery(id+"F0.wireOp",EDGE,"E11"),sQuery(id+"F0.wireOp",EDGE,"E12"),sQuery(id+"F0.wireOp",EDGE,"E13.filletArc"),sQuery(id+"F0.wireOp",EDGE,"E14.filletArc"),sQuery(id+"F0.wireOp",EDGE,"E15.0"),sQuery(id+"F0.wireOp",EDGE,"E15.1"),sQuery(id+"F0.wireOp",EDGE,"E15.3"),sQuery(id+"F0.wireOp",EDGE,"E15.4"),sQuery(id+"F0.wireOp",EDGE,"E15.5"),sQuery(id+"F0.wireOp",EDGE,"E16"),sQuery(id+"F0.wireOp",EDGE,"E17"),sQuery(id+"F0.wireOp",EDGE,"E19"),sQuery(id+"F0.wireOp",EDGE,"E21"),sQuery(id+"F0.wireOp",EDGE,"E23"),sQuery(id+"F0.wireOp",EDGE,"E24"),sQuery(id+"F0.wireOp",EDGE,"E25"),sQuery(id+"F0.wireOp",EDGE,"E26"),sQuery(id+"F0.wireOp",EDGE,"E27"),sQuery(id+"F0.wireOp",EDGE,"E28.0.1.0"),sQuery(id+"F0.wireOp",EDGE,"E28.0.2.0"),sQuery(id+"F0.wireOp",EDGE,"E28.0.3.0"),sQuery(id+"F0.wireOp",EDGE,"E28.0.4.0"),sQuery(id+"F0.wireOp",EDGE,"E28.0.5.0"),sQuery(id+"F0.wireOp",EDGE,"E28.0.6.0"),sQuery(id+"F0.wireOp",EDGE,"E28.0.7.0"),sQuery(id+"F0.wireOp",EDGE,"E28.0.8.0"),sQuery(id+"F0.wireOp",EDGE,"E28.0.9.0"),sQuery(id+"F0.wireOp",EDGE,"E28.0.10.0"),sQuery(id+"F0.wireOp",EDGE,"E28.0.11.0"),sQuery(id+"F0.wireOp",EDGE,"E28.0.12.0"),sQuery(id+"F0.wireOp",EDGE,"E28.0.13.0"),sQuery(id+"F0.wireOp",EDGE,"E28.0.14.0"),sQuery(id+"F0.wireOp",EDGE,"E28.0.15.0"),sQuery(id+"F0.wireOp",EDGE,"E28.0.16.0"),sQuery(id+"F0.wireOp",EDGE,"E28.0.17.0"),sQuery(id+"F0.wireOp",EDGE,"E28.0.18.0"),sQuery(id+"F0.wireOp",EDGE,"E29"),sQuery(id+"F0.wireOp",EDGE,"E30"),sQuery(id+"F0.wireOp",EDGE,"E31"),sQuery(id+"F0.wireOp",EDGE,"E32"),sQuery(id+"F0.wireOp",EDGE,"E36"),sQuery(id+"F0.wireOp",EDGE,"E37.0.1.0"),sQuery(id+"F0.wireOp",EDGE,"E37.0.2.0"),sQuery(id+"F0.wireOp",EDGE,"E37.0.3.0"),sQuery(id+"F0.wireOp",EDGE,"E37.0.4.0"),sQuery(id+"F0.wireOp",EDGE,"E37.0.5.0"),sQuery(id+"F0.wireOp",EDGE,"E37.0.6.0"),sQuery(id+"F0.wireOp",EDGE,"E37.0.7.0"),sQuery(id+"F0.wireOp",EDGE,"E37.0.8.0"),sQuery(id+"F0.wireOp",EDGE,"E37.0.9.0"),sQuery(id+"F0.wireOp",EDGE,"E37.0.10.0"),sQuery(id+"F0.wireOp",EDGE,"E37.0.11.0"),sQuery(id+"F0.wireOp",EDGE,"E37.0.12.0"),sQuery(id+"F0.wireOp",EDGE,"E38"),sQuery(id+"F0.wireOp",EDGE,"E42.0.0.13"),sQuery(id+"F0.wireOp",EDGE,"E59"),sQuery(id+"F0.wireOp",EDGE,"E60"),sQuery(id+"F0.wireOp",EDGE,"E61"),sQuery(id+"F0.wireOp",EDGE,"E62"),sQuery(id+"F0.wireOp",EDGE,"E63"),sQuery(id+"F0.wireOp",EDGE,"E64"),sQuery(id+"F0.wireOp",EDGE,"E65"),sQuery(id+"F0.wireOp",EDGE,"E66"),sQuery(id+"F0.wireOp",EDGE,"E67")])]});
            var Q1;
            Q1=makeQuery(id+"F6.opExtrude","SWEPT_BODY",BODY,{"disambiguationData":[OSD([sQuery(id+"F0.wireOp",EDGE,"E0"),sQuery(id+"F0.wireOp",EDGE,"E1"),sQuery(id+"F0.wireOp",EDGE,"E2"),sQuery(id+"F0.wireOp",EDGE,"E3"),sQuery(id+"F0.wireOp",EDGE,"E7"),sQuery(id+"F0.wireOp",EDGE,"E8"),sQuery(id+"F0.wireOp",EDGE,"E11"),sQuery(id+"F0.wireOp",EDGE,"E12"),sQuery(id+"F0.wireOp",EDGE,"E15.0"),sQuery(id+"F0.wireOp",EDGE,"E15.1"),sQuery(id+"F0.wireOp",EDGE,"E15.3"),sQuery(id+"F0.wireOp",EDGE,"E15.4"),sQuery(id+"F0.wireOp",EDGE,"E15.5"),sQuery(id+"F0.wireOp",EDGE,"E16"),sQuery(id+"F0.wireOp",EDGE,"E17"),sQuery(id+"F0.wireOp",EDGE,"E19"),sQuery(id+"F0.wireOp",EDGE,"E21"),sQuery(id+"F0.wireOp",EDGE,"E27"),sQuery(id+"F0.wireOp",EDGE,"E28.0.1.0"),sQuery(id+"F0.wireOp",EDGE,"E28.0.2.0"),sQuery(id+"F0.wireOp",EDGE,"E28.0.3.0"),sQuery(id+"F0.wireOp",EDGE,"E28.0.4.0"),sQuery(id+"F0.wireOp",EDGE,"E28.0.5.0"),sQuery(id+"F0.wireOp",EDGE,"E28.0.6.0"),sQuery(id+"F0.wireOp",EDGE,"E28.0.7.0"),sQuery(id+"F0.wireOp",EDGE,"E28.0.8.0"),sQuery(id+"F0.wireOp",EDGE,"E28.0.9.0"),sQuery(id+"F0.wireOp",EDGE,"E28.0.10.0"),sQuery(id+"F0.wireOp",EDGE,"E28.0.11.0"),sQuery(id+"F0.wireOp",EDGE,"E28.0.12.0"),sQuery(id+"F0.wireOp",EDGE,"E28.0.13.0"),sQuery(id+"F0.wireOp",EDGE,"E28.0.14.0"),sQuery(id+"F0.wireOp",EDGE,"E28.0.15.0"),sQuery(id+"F0.wireOp",EDGE,"E28.0.16.0"),sQuery(id+"F0.wireOp",EDGE,"E28.0.17.0"),sQuery(id+"F0.wireOp",EDGE,"E28.0.18.0"),sQuery(id+"F0.wireOp",EDGE,"E29"),sQuery(id+"F0.wireOp",EDGE,"E30"),sQuery(id+"F0.wireOp",EDGE,"E31"),sQuery(id+"F0.wireOp",EDGE,"E32"),sQuery(id+"F0.wireOp",EDGE,"E36"),sQuery(id+"F0.wireOp",EDGE,"E37.0.1.0"),sQuery(id+"F0.wireOp",EDGE,"E37.0.2.0"),sQuery(id+"F0.wireOp",EDGE,"E37.0.3.0"),sQuery(id+"F0.wireOp",EDGE,"E37.0.4.0"),sQuery(id+"F0.wireOp",EDGE,"E37.0.5.0"),sQuery(id+"F0.wireOp",EDGE,"E37.0.6.0"),sQuery(id+"F0.wireOp",EDGE,"E37.0.7.0"),sQuery(id+"F0.wireOp",EDGE,"E37.0.8.0"),sQuery(id+"F0.wireOp",EDGE,"E37.0.9.0"),sQuery(id+"F0.wireOp",EDGE,"E37.0.10.0"),sQuery(id+"F0.wireOp",EDGE,"E37.0.11.0"),sQuery(id+"F0.wireOp",EDGE,"E37.0.12.0"),sQuery(id+"F0.wireOp",EDGE,"E38"),sQuery(id+"F0.wireOp",EDGE,"E42.0.0.13"),sQuery(id+"F0.wireOp",EDGE,"E59"),sQuery(id+"F0.wireOp",EDGE,"E60"),sQuery(id+"F0.wireOp",EDGE,"E61"),sQuery(id+"F0.wireOp",EDGE,"E62"),sQuery(id+"F0.wireOp",EDGE,"E63"),sQuery(id+"F0.wireOp",EDGE,"E64"),sQuery(id+"F0.wireOp",EDGE,"E65"),sQuery(id+"F0.wireOp",EDGE,"E66"),sQuery(id+"F0.wireOp",EDGE,"E67")])]});
            var Q2;
            Q2=makeQuery(id+"F3.opExtrude","SWEPT_BODY",BODY,{"disambiguationData":[OSD([sQuery(id+"F0.wireOp",EDGE,"E0"),sQuery(id+"F0.wireOp",EDGE,"E1"),sQuery(id+"F0.wireOp",EDGE,"E3"),sQuery(id+"F0.wireOp",EDGE,"E10.filletArc"),sQuery(id+"F0.wireOp",EDGE,"E15.0"),sQuery(id+"F0.wireOp",EDGE,"E15.1"),sQuery(id+"F0.wireOp",EDGE,"E15.2"),sQuery(id+"F0.wireOp",EDGE,"E17"),sQuery(id+"F0.wireOp",EDGE,"E19")])]});
            booleanBodies(context, id + "F14", {"operationType" : BooleanOperationType.SUBTRACTION, "tools" : qUnion([Q0, Q1]), "targets" : qUnion([Q2]), "keepTools" : true});
        }
        {
            var Q0;
            Q0=makeQuery(id+"F2.opExtrude","SWEPT_FACE",FACE,{"disambiguationData":[OSD([sQuery(id+"F0.wireOp",EDGE,"E3")])]});
            var sketch = newSketch(context, id + "F15", { "sketchPlane" : qUnion([Q0])});
            skLineSegment(sketch, "E84.bottom", {"start": v(-74, 200) * mm, "end": v(-64, 200) * mm});
            skLineSegment(sketch, "E84.top", {"start": v(-74, 197) * mm, "end": v(-64, 197) * mm});
            skLineSegment(sketch, "E84.left", {"start": v(-74, 200) * mm, "end": v(-74, 197) * mm});
            skLineSegment(sketch, "E84.right", {"start": v(-64, 200) * mm, "end": v(-64, 197) * mm});
            skLineSegment(sketch, "E85.bottom", {"start": v(-74, 3) * mm, "end": v(-64, 3) * mm});
            skLineSegment(sketch, "E85.top", {"start": v(-74, 0) * mm, "end": v(-64, 0) * mm});
            skLineSegment(sketch, "E85.left", {"start": v(-74, 3) * mm, "end": v(-74, 0) * mm});
            skLineSegment(sketch, "E85.right", {"start": v(-64, 3) * mm, "end": v(-64, 0) * mm});
            skLineSegment(sketch, "E86.1.0.0", {"start": v(-54, 200) * mm, "end": v(-44, 200) * mm});
            skLineSegment(sketch, "E86.1.0.1", {"start": v(-54, 197) * mm, "end": v(-44, 197) * mm});
            skLineSegment(sketch, "E86.1.0.2", {"start": v(-54, 0) * mm, "end": v(-44, 0) * mm});
            skLineSegment(sketch, "E86.1.0.3", {"start": v(-54, 3) * mm, "end": v(-44, 3) * mm});
            skLineSegment(sketch, "E86.1.0.4", {"start": v(-54, 200) * mm, "end": v(-54, 197) * mm});
            skLineSegment(sketch, "E86.1.0.5", {"start": v(-44, 200) * mm, "end": v(-44, 197) * mm});
            skLineSegment(sketch, "E86.1.0.6", {"start": v(-54, 3) * mm, "end": v(-54, 0) * mm});
            skLineSegment(sketch, "E86.1.0.7", {"start": v(-44, 3) * mm, "end": v(-44, 0) * mm});
            skLineSegment(sketch, "E86.2.0.0", {"start": v(-34, 200) * mm, "end": v(-24, 200) * mm});
            skLineSegment(sketch, "E86.2.0.1", {"start": v(-34, 197) * mm, "end": v(-24, 197) * mm});
            skLineSegment(sketch, "E86.2.0.2", {"start": v(-34, 0) * mm, "end": v(-24, 0) * mm});
            skLineSegment(sketch, "E86.2.0.3", {"start": v(-34, 3) * mm, "end": v(-24, 3) * mm});
            skLineSegment(sketch, "E86.2.0.4", {"start": v(-34, 200) * mm, "end": v(-34, 197) * mm});
            skLineSegment(sketch, "E86.2.0.5", {"start": v(-24, 200) * mm, "end": v(-24, 197) * mm});
            skLineSegment(sketch, "E86.2.0.6", {"start": v(-34, 3) * mm, "end": v(-34, 0) * mm});
            skLineSegment(sketch, "E86.2.0.7", {"start": v(-24, 3) * mm, "end": v(-24, 0) * mm});
            skLineSegment(sketch, "E86.3.0.0", {"start": v(-14, 200) * mm, "end": v(-4, 200) * mm});
            skLineSegment(sketch, "E86.3.0.1", {"start": v(-14, 197) * mm, "end": v(-4, 197) * mm});
            skLineSegment(sketch, "E86.3.0.2", {"start": v(-14, 0) * mm, "end": v(-4, 0) * mm});
            skLineSegment(sketch, "E86.3.0.3", {"start": v(-14, 3) * mm, "end": v(-4, 3) * mm});
            skLineSegment(sketch, "E86.3.0.4", {"start": v(-14, 200) * mm, "end": v(-14, 197) * mm});
            skLineSegment(sketch, "E86.3.0.5", {"start": v(-4, 200) * mm, "end": v(-4, 197) * mm});
            skLineSegment(sketch, "E86.3.0.6", {"start": v(-14, 3) * mm, "end": v(-14, 0) * mm});
            skLineSegment(sketch, "E86.3.0.7", {"start": v(-4, 3) * mm, "end": v(-4, 0) * mm});
            skLineSegment(sketch, "E86.direction1", {"start": v(-74, 0) * mm, "end": v(-54, 0) * mm, "construction": true});
            skLineSegment(sketch, "E87.bottom", {"start": v(-24, 150) * mm, "end": v(-14, 150) * mm});
            skLineSegment(sketch, "E87.top", {"start": v(-24, 146) * mm, "end": v(-14, 146) * mm});
            skLineSegment(sketch, "E87.left", {"start": v(-24, 150) * mm, "end": v(-24, 146) * mm});
            skLineSegment(sketch, "E87.right", {"start": v(-14, 150) * mm, "end": v(-14, 146) * mm});
            skLineSegment(sketch, "E88.1.0.0", {"start": v(-44, 150) * mm, "end": v(-44, 146) * mm});
            skLineSegment(sketch, "E88.1.0.1", {"start": v(-44, 150) * mm, "end": v(-34, 150) * mm});
            skLineSegment(sketch, "E88.1.0.2", {"start": v(-44, 146) * mm, "end": v(-34, 146) * mm});
            skLineSegment(sketch, "E88.1.0.3", {"start": v(-34, 150) * mm, "end": v(-34, 146) * mm});
            skLineSegment(sketch, "E88.2.0.0", {"start": v(-64, 150) * mm, "end": v(-64, 146) * mm});
            skLineSegment(sketch, "E88.2.0.1", {"start": v(-64, 150) * mm, "end": v(-54, 150) * mm});
            skLineSegment(sketch, "E88.2.0.2", {"start": v(-64, 146) * mm, "end": v(-54, 146) * mm});
            skLineSegment(sketch, "E88.2.0.3", {"start": v(-54, 150) * mm, "end": v(-54, 146) * mm});
            skLineSegment(sketch, "E88.direction1", {"start": v(-24, 146) * mm, "end": v(-44, 146) * mm, "construction": true});
            skSolve(sketch);
        }
        {
            var Q0;
            Q0=makeQuery(id+"F15.imprint","IMPRINT",FACE,{"disambiguationData":[TD([[makeQuery(id+"F15.imprint","IMPRINT",EDGE,{"derivedFrom":sQuery(id+"F15.wireOp",EDGE,"E84.bottom")}),-1.0]])]});
            var Q1;
            Q1=makeQuery(id+"F15.imprint","IMPRINT",FACE,{"disambiguationData":[TD([[makeQuery(id+"F15.imprint","IMPRINT",EDGE,{"derivedFrom":sQuery(id+"F15.wireOp",EDGE,"E85.bottom")}),-1.0]])]});
            var Q2;
            Q2=makeQuery(id+"F15.imprint","IMPRINT",FACE,{"disambiguationData":[TD([[makeQuery(id+"F15.imprint","IMPRINT",EDGE,{"derivedFrom":sQuery(id+"F15.wireOp",EDGE,"E86.1.0.0")}),-1.0]])]});
            var Q3;
            Q3=makeQuery(id+"F15.imprint","IMPRINT",FACE,{"disambiguationData":[TD([[makeQuery(id+"F15.imprint","IMPRINT",EDGE,{"derivedFrom":sQuery(id+"F15.wireOp",EDGE,"E86.1.0.2")}),1.0]])]});
            var Q4;
            Q4=makeQuery(id+"F15.imprint","IMPRINT",FACE,{"disambiguationData":[TD([[makeQuery(id+"F15.imprint","IMPRINT",EDGE,{"derivedFrom":sQuery(id+"F15.wireOp",EDGE,"E86.2.0.0")}),-1.0]])]});
            var Q5;
            Q5=makeQuery(id+"F15.imprint","IMPRINT",FACE,{"disambiguationData":[TD([[makeQuery(id+"F15.imprint","IMPRINT",EDGE,{"derivedFrom":sQuery(id+"F15.wireOp",EDGE,"E86.2.0.2")}),1.0]])]});
            var Q6;
            Q6=makeQuery(id+"F15.imprint","IMPRINT",FACE,{"disambiguationData":[TD([[makeQuery(id+"F15.imprint","IMPRINT",EDGE,{"derivedFrom":sQuery(id+"F15.wireOp",EDGE,"E86.3.0.0")}),-1.0]])]});
            var Q7;
            Q7=makeQuery(id+"F15.imprint","IMPRINT",FACE,{"disambiguationData":[TD([[makeQuery(id+"F15.imprint","IMPRINT",EDGE,{"derivedFrom":sQuery(id+"F15.wireOp",EDGE,"E86.3.0.2")}),1.0]])]});
            var Q8;
            Q8=makeQuery(id+"F15.imprint","IMPRINT",FACE,{"disambiguationData":[TD([[makeQuery(id+"F15.imprint","IMPRINT",EDGE,{"derivedFrom":sQuery(id+"F15.wireOp",EDGE,"E88.2.0.0")}),1.0]])]});
            var Q9;
            Q9=makeQuery(id+"F15.imprint","IMPRINT",FACE,{"disambiguationData":[TD([[makeQuery(id+"F15.imprint","IMPRINT",EDGE,{"derivedFrom":sQuery(id+"F15.wireOp",EDGE,"E88.1.0.0")}),1.0]])]});
            var Q10;
            Q10=makeQuery(id+"F15.imprint","IMPRINT",FACE,{"disambiguationData":[TD([[makeQuery(id+"F15.imprint","IMPRINT",EDGE,{"derivedFrom":sQuery(id+"F15.wireOp",EDGE,"E87.bottom")}),-1.0]])]});
            extrude(context, id + "F16", {"entities" : qUnion([Q0, Q1, Q2, Q3, Q4, Q5, Q6, Q7, Q8, Q9, Q10]), "operationType" : NewBodyOperationType.REMOVE, "oppositeDirection" : true, "depth" : 3 * mm, "offsetDistance" : 25 * mm});
        }
        {
            var Q0;
            Q0=makeQuery(id+"F2.opExtrude","SWEPT_BODY",BODY,{"disambiguationData":[OSD([sQuery(id+"F0.wireOp",EDGE,"E0"),sQuery(id+"F0.wireOp",EDGE,"E2"),sQuery(id+"F0.wireOp",EDGE,"E3"),sQuery(id+"F0.wireOp",EDGE,"E15.3"),sQuery(id+"F0.wireOp",EDGE,"E34"),sQuery(id+"F0.wireOp",EDGE,"E35")])]});
            var Q1;
            Q1=makeQuery(id+"F3.opExtrude","SWEPT_BODY",BODY,{"disambiguationData":[OSD([sQuery(id+"F0.wireOp",EDGE,"E0"),sQuery(id+"F0.wireOp",EDGE,"E1"),sQuery(id+"F0.wireOp",EDGE,"E3"),sQuery(id+"F0.wireOp",EDGE,"E10.filletArc"),sQuery(id+"F0.wireOp",EDGE,"E15.0"),sQuery(id+"F0.wireOp",EDGE,"E15.1"),sQuery(id+"F0.wireOp",EDGE,"E15.2"),sQuery(id+"F0.wireOp",EDGE,"E17"),sQuery(id+"F0.wireOp",EDGE,"E19")])]});
            var Q2;
            Q2=makeQuery(id+"F3.opExtrude","SWEPT_BODY",BODY,{"disambiguationData":[OSD([sQuery(id+"F0.wireOp",EDGE,"E2"),sQuery(id+"F0.wireOp",EDGE,"E3"),sQuery(id+"F0.wireOp",EDGE,"E7"),sQuery(id+"F0.wireOp",EDGE,"E9.filletArc"),sQuery(id+"F0.wireOp",EDGE,"E15.4"),sQuery(id+"F0.wireOp",EDGE,"E15.5"),sQuery(id+"F0.wireOp",EDGE,"E15.9"),sQuery(id+"F0.wireOp",EDGE,"E18"),sQuery(id+"F0.wireOp",EDGE,"E59")])]});
            booleanBodies(context, id + "F17", {"operationType" : BooleanOperationType.SUBTRACTION, "tools" : qUnion([Q0]), "targets" : qUnion([Q1, Q2]), "keepTools" : true});
        }
        {
            var Q0;
            Q0=makeQuery(id+"F1.opExtrude","SWEPT_FACE",FACE,{"disambiguationData":[OSD([sQuery(id+"F0.wireOp",EDGE,"E68.top")])]});
            var sketch = newSketch(context, id + "F18", { "sketchPlane" : qUnion([Q0])});
            skLineSegment(sketch, "E89.bottom", {"start": v(0, 120) * mm, "end": v(78, 120) * mm});
            skLineSegment(sketch, "E89.top", {"start": v(0, -3) * mm, "end": v(78, -3) * mm});
            skLineSegment(sketch, "E89.left", {"start": v(0, 120) * mm, "end": v(0, -3) * mm});
            skLineSegment(sketch, "E89.right", {"start": v(78, 120) * mm, "end": v(78, 85) * mm});
            skArc(sketch, "E90", {"start": v(52.55, 82.22) * mm, "mid": v(32.92, 89.25) * mm, "end": v(20.5, 72.5) * mm});
            skArc(sketch, "E91", {"start": v(20.5, 47.5) * mm, "mid": v(32.92, 30.75) * mm, "end": v(52.55, 37.78) * mm});
            skLineSegment(sketch, "E92", {"start": v(20.5, 72.5) * mm, "end": v(20.5, 47.5) * mm});
            skLineSegment(sketch, "E93", {"start": v(56.7, 80) * mm, "end": v(73, 80) * mm});
            skLineSegment(sketch, "E94", {"start": v(56.7, 40) * mm, "end": v(73, 40) * mm});
            skLineSegment(sketch, "E95.trimOffspring", {"start": v(78, 35) * mm, "end": v(78, -3) * mm});
            skPoint(sketch, "E96.visualSharp", {"position": v(53.81, 80) * mm});
            skArc(sketch, "E96.filletArc", {"start": v(52.55, 82.22) * mm, "mid": v(54.35, 80.6) * mm, "end": v(56.7, 80) * mm});
            skPoint(sketch, "E97.visualSharp", {"position": v(53.81, 40) * mm});
            skArc(sketch, "E97.filletArc", {"start": v(56.7, 40) * mm, "mid": v(54.35, 39.4) * mm, "end": v(52.55, 37.78) * mm});
            skPoint(sketch, "E98.visualSharp", {"position": v(78, 40) * mm});
            skArc(sketch, "E98.filletArc", {"start": v(78, 35) * mm, "mid": v(76.54, 38.54) * mm, "end": v(73, 40) * mm});
            skPoint(sketch, "E99.visualSharp", {"position": v(78, 80) * mm});
            skArc(sketch, "E99.filletArc", {"start": v(73, 80) * mm, "mid": v(76.54, 81.46) * mm, "end": v(78, 85) * mm});
            skSolve(sketch);
        }
        {
            var Q0;
            Q0=makeQuery(id+"F1.opExtrude","SWEPT_FACE",FACE,{"disambiguationData":[OSD([sQuery(id+"F0.wireOp",EDGE,"E5")])]});
            var sketch = newSketch(context, id + "F19", { "sketchPlane" : qUnion([Q0])});
            skLineSegment(sketch, "E100.bottom", {"start": v(0, 150) * mm, "end": v(-78, 150) * mm});
            skLineSegment(sketch, "E100.top", {"start": v(0, 50) * mm, "end": v(-4, 50) * mm});
            skLineSegment(sketch, "E100.left", {"start": v(0, 150) * mm, "end": v(0, 50) * mm});
            skLineSegment(sketch, "E100.right", {"start": v(-78, 150) * mm, "end": v(-78, 146) * mm});
            skLineSegment(sketch, "E101.bottom", {"start": v(0, 135) * mm, "end": v(-4, 135) * mm});
            skLineSegment(sketch, "E101.top", {"start": v(0, 125) * mm, "end": v(-4, 125) * mm});
            skLineSegment(sketch, "E101.left", {"start": v(0, 135) * mm, "end": v(0, 125) * mm});
            skLineSegment(sketch, "E101.right", {"start": v(-4, 135) * mm, "end": v(-4, 125) * mm});
            skLineSegment(sketch, "E102.0.1.0", {"start": v(0, 105) * mm, "end": v(-4, 105) * mm});
            skLineSegment(sketch, "E102.0.1.1", {"start": v(-4, 115) * mm, "end": v(-4, 105) * mm});
            skLineSegment(sketch, "E102.0.1.2", {"start": v(0, 115) * mm, "end": v(-4, 115) * mm});
            skLineSegment(sketch, "E102.0.1.3", {"start": v(0, 115) * mm, "end": v(0, 105) * mm});
            skLineSegment(sketch, "E102.0.2.0", {"start": v(0, 85) * mm, "end": v(-4, 85) * mm});
            skLineSegment(sketch, "E102.0.2.1", {"start": v(-4, 95) * mm, "end": v(-4, 85) * mm});
            skLineSegment(sketch, "E102.0.2.2", {"start": v(0, 95) * mm, "end": v(-4, 95) * mm});
            skLineSegment(sketch, "E102.0.2.3", {"start": v(0, 95) * mm, "end": v(0, 85) * mm});
            skLineSegment(sketch, "E102.0.3.0", {"start": v(0, 65) * mm, "end": v(-4, 65) * mm});
            skLineSegment(sketch, "E102.0.3.1", {"start": v(-4, 75) * mm, "end": v(-4, 65) * mm});
            skLineSegment(sketch, "E102.0.3.2", {"start": v(0, 75) * mm, "end": v(-4, 75) * mm});
            skLineSegment(sketch, "E102.0.3.3", {"start": v(0, 75) * mm, "end": v(0, 65) * mm});
            skLineSegment(sketch, "E102.direction1", {"start": v(-4, 125) * mm, "end": v(21, 125) * mm, "construction": true});
            skLineSegment(sketch, "E102.direction2", {"start": v(-4, 125) * mm, "end": v(-4, 105) * mm, "construction": true});
            skLineSegment(sketch, "E103.bottom", {"start": v(-22, 150) * mm, "end": v(-12, 150) * mm});
            skLineSegment(sketch, "E103.top", {"start": v(-22, 146) * mm, "end": v(-12, 146) * mm});
            skLineSegment(sketch, "E103.left", {"start": v(-22, 150) * mm, "end": v(-22, 146) * mm});
            skLineSegment(sketch, "E103.right", {"start": v(-12, 150) * mm, "end": v(-12, 146) * mm});
            skLineSegment(sketch, "E104.1.0.0", {"start": v(-42, 146) * mm, "end": v(-32, 146) * mm});
            skLineSegment(sketch, "E104.1.0.1", {"start": v(-32, 150) * mm, "end": v(-32, 146) * mm});
            skLineSegment(sketch, "E104.1.0.2", {"start": v(-42, 150) * mm, "end": v(-32, 150) * mm});
            skLineSegment(sketch, "E104.1.0.3", {"start": v(-42, 150) * mm, "end": v(-42, 146) * mm});
            skLineSegment(sketch, "E104.2.0.0", {"start": v(-62, 146) * mm, "end": v(-52, 146) * mm});
            skLineSegment(sketch, "E104.2.0.1", {"start": v(-52, 150) * mm, "end": v(-52, 146) * mm});
            skLineSegment(sketch, "E104.2.0.2", {"start": v(-62, 150) * mm, "end": v(-52, 150) * mm});
            skLineSegment(sketch, "E104.2.0.3", {"start": v(-62, 150) * mm, "end": v(-62, 146) * mm});
            skLineSegment(sketch, "E104.direction1", {"start": v(-22, 146) * mm, "end": v(-42, 146) * mm, "construction": true});
            skLineSegment(sketch, "E105.0.3.0", {"start": v(-78, 146) * mm, "end": v(-72, 146) * mm});
            skLineSegment(sketch, "E105.3.3.0", {"start": v(-72, 150) * mm, "end": v(-72, 146) * mm});
            skLineSegment(sketch, "E105.6.3.0", {"start": v(-78, 150) * mm, "end": v(-72, 150) * mm});
            skArc(sketch, "E106", {"start": v(-78, 146) * mm, "mid": v(-57.35, 85.4) * mm, "end": v(-4, 50) * mm});
            skLineSegment(sketch, "E107.bottom", {"start": v(0, 150) * mm, "end": v(-4, 150) * mm});
            skLineSegment(sketch, "E107.top", {"start": v(0, 146) * mm, "end": v(-4, 146) * mm});
            skLineSegment(sketch, "E107.left", {"start": v(0, 150) * mm, "end": v(0, 146) * mm});
            skLineSegment(sketch, "E107.right", {"start": v(-4, 150) * mm, "end": v(-4, 146) * mm});
            skSolve(sketch);
        }
        {
            var Q0;
            {var subQ0=sQuery(id+"F19.wireOp",EDGE,"E100.top");Q0=makeQuery(id+"F19.imprint","IMPRINT",FACE,{"disambiguationData":[TD([[makeQuery(id+"F19.imprint","IMPRINT",EDGE,{"derivedFrom":subQ0}),-1.0]])]});}
            var Q1;
            {var subQ0=sQuery(id+"F19.wireOp",EDGE,"E102.0.2.0");Q1=makeQuery(id+"F19.imprint","IMPRINT",FACE,{"disambiguationData":[TD([[makeQuery(id+"F19.imprint","IMPRINT",EDGE,{"derivedFrom":subQ0}),1.0]])]});}
            var Q2;
            {var subQ0=sQuery(id+"F19.wireOp",EDGE,"E102.0.1.0");Q2=makeQuery(id+"F19.imprint","IMPRINT",FACE,{"disambiguationData":[TD([[makeQuery(id+"F19.imprint","IMPRINT",EDGE,{"derivedFrom":subQ0}),1.0]])]});}
            var Q3;
            {var subQ0=sQuery(id+"F19.wireOp",EDGE,"E101.top");Q3=makeQuery(id+"F19.imprint","IMPRINT",FACE,{"disambiguationData":[TD([[makeQuery(id+"F19.imprint","IMPRINT",EDGE,{"derivedFrom":subQ0}),1.0]])]});}
            var Q4;
            {var subQ2=sQuery(id+"F19.wireOp",EDGE,"E101.bottom");Q4=makeQuery(id+"F19.imprint","IMPRINT",FACE,{"disambiguationData":[TD([[makeQuery(id+"F19.imprint","IMPRINT",EDGE,{"derivedFrom":subQ2}),-1.0]])]});}
            var Q5;
            {var subQ11=sQuery(id+"F19.wireOp",EDGE,"E101.right");Q5=makeQuery(id+"F19.imprint","IMPRINT",FACE,{"disambiguationData":[TD([[makeQuery(id+"F19.imprint","IMPRINT",EDGE,{"derivedFrom":subQ11}),1.0]])]});}
            extrude(context, id + "F20", {"entities" : qUnion([Q0, Q1, Q2, Q3, Q4, Q5]), "oppositeDirection" : true, "depth" : 3 * mm, "offsetDistance" : 25 * mm});
        }
        {
            var Q0;
            Q0 = qSketchRegion(id + "F18", true);
            extrude(context, id + "F21", {"entities" : qUnion([Q0]), "depth" : 4 * mm, "offsetDistance" : 25 * mm});
        }
        {
            var Q0;
            Q0=makeQuery(id+"F20.opExtrude","SWEPT_BODY",BODY,{"disambiguationData":[OSD([sQuery(id+"F19.wireOp",EDGE,"E100.bottom"),sQuery(id+"F19.wireOp",EDGE,"E100.top"),sQuery(id+"F19.wireOp",EDGE,"E100.left"),sQuery(id+"F19.wireOp",EDGE,"E101.bottom"),sQuery(id+"F19.wireOp",EDGE,"E101.top"),sQuery(id+"F19.wireOp",EDGE,"E101.right"),sQuery(id+"F19.wireOp",EDGE,"E102.0.1.0"),sQuery(id+"F19.wireOp",EDGE,"E102.0.1.1"),sQuery(id+"F19.wireOp",EDGE,"E102.0.1.2"),sQuery(id+"F19.wireOp",EDGE,"E102.0.2.0"),sQuery(id+"F19.wireOp",EDGE,"E102.0.2.1"),sQuery(id+"F19.wireOp",EDGE,"E102.0.2.2"),sQuery(id+"F19.wireOp",EDGE,"E102.0.3.0"),sQuery(id+"F19.wireOp",EDGE,"E102.0.3.1"),sQuery(id+"F19.wireOp",EDGE,"E102.0.3.2"),sQuery(id+"F19.wireOp",EDGE,"E103.top"),sQuery(id+"F19.wireOp",EDGE,"E103.left"),sQuery(id+"F19.wireOp",EDGE,"E103.right"),sQuery(id+"F19.wireOp",EDGE,"E104.1.0.0"),sQuery(id+"F19.wireOp",EDGE,"E104.1.0.1"),sQuery(id+"F19.wireOp",EDGE,"E104.1.0.3"),sQuery(id+"F19.wireOp",EDGE,"E104.2.0.0"),sQuery(id+"F19.wireOp",EDGE,"E104.2.0.1"),sQuery(id+"F19.wireOp",EDGE,"E104.2.0.3"),sQuery(id+"F19.wireOp",EDGE,"E105.0.3.0"),sQuery(id+"F19.wireOp",EDGE,"E105.3.3.0"),sQuery(id+"F19.wireOp",EDGE,"E106"),sQuery(id+"F19.wireOp",EDGE,"E107.top"),sQuery(id+"F19.wireOp",EDGE,"E107.right")])]});
            var Q1;
            Q1=makeQuery(id+"F1.opExtrude","SWEPT_BODY",BODY,{"disambiguationData":[OSD([sQuery(id+"F0.wireOp",EDGE,"E0"),sQuery(id+"F0.wireOp",EDGE,"E1"),sQuery(id+"F0.wireOp",EDGE,"E2"),sQuery(id+"F0.wireOp",EDGE,"E3"),sQuery(id+"F0.wireOp",EDGE,"E4"),sQuery(id+"F0.wireOp",EDGE,"E5"),sQuery(id+"F0.wireOp",EDGE,"E6"),sQuery(id+"F0.wireOp",EDGE,"E7"),sQuery(id+"F0.wireOp",EDGE,"E8"),sQuery(id+"F0.wireOp",EDGE,"E11"),sQuery(id+"F0.wireOp",EDGE,"E12"),sQuery(id+"F0.wireOp",EDGE,"E13.filletArc"),sQuery(id+"F0.wireOp",EDGE,"E14.filletArc"),sQuery(id+"F0.wireOp",EDGE,"E15.0"),sQuery(id+"F0.wireOp",EDGE,"E15.1"),sQuery(id+"F0.wireOp",EDGE,"E15.3"),sQuery(id+"F0.wireOp",EDGE,"E15.4"),sQuery(id+"F0.wireOp",EDGE,"E15.5"),sQuery(id+"F0.wireOp",EDGE,"E16"),sQuery(id+"F0.wireOp",EDGE,"E17"),sQuery(id+"F0.wireOp",EDGE,"E19"),sQuery(id+"F0.wireOp",EDGE,"E21"),sQuery(id+"F0.wireOp",EDGE,"E23"),sQuery(id+"F0.wireOp",EDGE,"E24"),sQuery(id+"F0.wireOp",EDGE,"E25"),sQuery(id+"F0.wireOp",EDGE,"E26"),sQuery(id+"F0.wireOp",EDGE,"E27"),sQuery(id+"F0.wireOp",EDGE,"E28.0.1.0"),sQuery(id+"F0.wireOp",EDGE,"E28.0.2.0"),sQuery(id+"F0.wireOp",EDGE,"E28.0.3.0"),sQuery(id+"F0.wireOp",EDGE,"E28.0.4.0"),sQuery(id+"F0.wireOp",EDGE,"E28.0.5.0"),sQuery(id+"F0.wireOp",EDGE,"E28.0.6.0"),sQuery(id+"F0.wireOp",EDGE,"E28.0.7.0"),sQuery(id+"F0.wireOp",EDGE,"E28.0.8.0"),sQuery(id+"F0.wireOp",EDGE,"E28.0.9.0"),sQuery(id+"F0.wireOp",EDGE,"E28.0.10.0"),sQuery(id+"F0.wireOp",EDGE,"E28.0.11.0"),sQuery(id+"F0.wireOp",EDGE,"E28.0.12.0"),sQuery(id+"F0.wireOp",EDGE,"E28.0.13.0"),sQuery(id+"F0.wireOp",EDGE,"E28.0.14.0"),sQuery(id+"F0.wireOp",EDGE,"E28.0.15.0"),sQuery(id+"F0.wireOp",EDGE,"E28.0.16.0"),sQuery(id+"F0.wireOp",EDGE,"E28.0.17.0"),sQuery(id+"F0.wireOp",EDGE,"E28.0.18.0"),sQuery(id+"F0.wireOp",EDGE,"E29"),sQuery(id+"F0.wireOp",EDGE,"E30"),sQuery(id+"F0.wireOp",EDGE,"E31"),sQuery(id+"F0.wireOp",EDGE,"E32"),sQuery(id+"F0.wireOp",EDGE,"E36"),sQuery(id+"F0.wireOp",EDGE,"E37.0.1.0"),sQuery(id+"F0.wireOp",EDGE,"E37.0.2.0"),sQuery(id+"F0.wireOp",EDGE,"E37.0.3.0"),sQuery(id+"F0.wireOp",EDGE,"E37.0.4.0"),sQuery(id+"F0.wireOp",EDGE,"E37.0.5.0"),sQuery(id+"F0.wireOp",EDGE,"E37.0.6.0"),sQuery(id+"F0.wireOp",EDGE,"E37.0.7.0"),sQuery(id+"F0.wireOp",EDGE,"E37.0.8.0"),sQuery(id+"F0.wireOp",EDGE,"E37.0.9.0"),sQuery(id+"F0.wireOp",EDGE,"E37.0.10.0"),sQuery(id+"F0.wireOp",EDGE,"E37.0.11.0"),sQuery(id+"F0.wireOp",EDGE,"E37.0.12.0"),sQuery(id+"F0.wireOp",EDGE,"E38"),sQuery(id+"F0.wireOp",EDGE,"E42.0.0.13"),sQuery(id+"F0.wireOp",EDGE,"E59"),sQuery(id+"F0.wireOp",EDGE,"E60"),sQuery(id+"F0.wireOp",EDGE,"E61"),sQuery(id+"F0.wireOp",EDGE,"E62"),sQuery(id+"F0.wireOp",EDGE,"E63"),sQuery(id+"F0.wireOp",EDGE,"E64"),sQuery(id+"F0.wireOp",EDGE,"E65"),sQuery(id+"F0.wireOp",EDGE,"E66"),sQuery(id+"F0.wireOp",EDGE,"E67"),sQuery(id+"F0.wireOp",EDGE,"E68.bottom"),sQuery(id+"F0.wireOp",EDGE,"E68.top"),sQuery(id+"F0.wireOp",EDGE,"E68.left"),sQuery(id+"F0.wireOp",EDGE,"E68.right"),sQuery(id+"F0.wireOp",EDGE,"E69.1.0.0"),sQuery(id+"F0.wireOp",EDGE,"E69.1.0.1"),sQuery(id+"F0.wireOp",EDGE,"E69.1.0.2"),sQuery(id+"F0.wireOp",EDGE,"E69.1.0.3"),sQuery(id+"F0.wireOp",EDGE,"E69.2.0.0"),sQuery(id+"F0.wireOp",EDGE,"E69.2.0.1"),sQuery(id+"F0.wireOp",EDGE,"E69.2.0.2"),sQuery(id+"F0.wireOp",EDGE,"E69.2.0.3"),sQuery(id+"F0.wireOp",EDGE,"E69.3.0.0"),sQuery(id+"F0.wireOp",EDGE,"E69.3.0.1"),sQuery(id+"F0.wireOp",EDGE,"E69.3.0.2"),sQuery(id+"F0.wireOp",EDGE,"E69.3.0.3"),sQuery(id+"F0.wireOp",EDGE,"E69.4.0.0"),sQuery(id+"F0.wireOp",EDGE,"E69.4.0.1"),sQuery(id+"F0.wireOp",EDGE,"E69.4.0.2"),sQuery(id+"F0.wireOp",EDGE,"E69.4.0.3"),sQuery(id+"F0.wireOp",EDGE,"E69.5.0.0"),sQuery(id+"F0.wireOp",EDGE,"E69.5.0.1"),sQuery(id+"F0.wireOp",EDGE,"E69.5.0.2"),sQuery(id+"F0.wireOp",EDGE,"E69.5.0.3")])]});
            booleanBodies(context, id + "F22", {"operationType" : BooleanOperationType.SUBTRACTION, "tools" : qUnion([Q0]), "targets" : qUnion([Q1]), "keepTools" : true});
        }
        {
            var Q0;
            Q0=makeQuery(id+"F2.opExtrude","SWEPT_BODY",BODY,{"disambiguationData":[OSD([sQuery(id+"F0.wireOp",EDGE,"E0"),sQuery(id+"F0.wireOp",EDGE,"E2"),sQuery(id+"F0.wireOp",EDGE,"E3"),sQuery(id+"F0.wireOp",EDGE,"E15.3"),sQuery(id+"F0.wireOp",EDGE,"E34"),sQuery(id+"F0.wireOp",EDGE,"E35")])]});
            var Q1;
            Q1=makeQuery(id+"F1.opExtrude","SWEPT_BODY",BODY,{"disambiguationData":[OSD([sQuery(id+"F0.wireOp",EDGE,"E0"),sQuery(id+"F0.wireOp",EDGE,"E1"),sQuery(id+"F0.wireOp",EDGE,"E2"),sQuery(id+"F0.wireOp",EDGE,"E3"),sQuery(id+"F0.wireOp",EDGE,"E4"),sQuery(id+"F0.wireOp",EDGE,"E5"),sQuery(id+"F0.wireOp",EDGE,"E6"),sQuery(id+"F0.wireOp",EDGE,"E7"),sQuery(id+"F0.wireOp",EDGE,"E8"),sQuery(id+"F0.wireOp",EDGE,"E11"),sQuery(id+"F0.wireOp",EDGE,"E12"),sQuery(id+"F0.wireOp",EDGE,"E13.filletArc"),sQuery(id+"F0.wireOp",EDGE,"E14.filletArc"),sQuery(id+"F0.wireOp",EDGE,"E15.0"),sQuery(id+"F0.wireOp",EDGE,"E15.1"),sQuery(id+"F0.wireOp",EDGE,"E15.3"),sQuery(id+"F0.wireOp",EDGE,"E15.4"),sQuery(id+"F0.wireOp",EDGE,"E15.5"),sQuery(id+"F0.wireOp",EDGE,"E16"),sQuery(id+"F0.wireOp",EDGE,"E17"),sQuery(id+"F0.wireOp",EDGE,"E19"),sQuery(id+"F0.wireOp",EDGE,"E21"),sQuery(id+"F0.wireOp",EDGE,"E23"),sQuery(id+"F0.wireOp",EDGE,"E24"),sQuery(id+"F0.wireOp",EDGE,"E25"),sQuery(id+"F0.wireOp",EDGE,"E26"),sQuery(id+"F0.wireOp",EDGE,"E27"),sQuery(id+"F0.wireOp",EDGE,"E28.0.1.0"),sQuery(id+"F0.wireOp",EDGE,"E28.0.2.0"),sQuery(id+"F0.wireOp",EDGE,"E28.0.3.0"),sQuery(id+"F0.wireOp",EDGE,"E28.0.4.0"),sQuery(id+"F0.wireOp",EDGE,"E28.0.5.0"),sQuery(id+"F0.wireOp",EDGE,"E28.0.6.0"),sQuery(id+"F0.wireOp",EDGE,"E28.0.7.0"),sQuery(id+"F0.wireOp",EDGE,"E28.0.8.0"),sQuery(id+"F0.wireOp",EDGE,"E28.0.9.0"),sQuery(id+"F0.wireOp",EDGE,"E28.0.10.0"),sQuery(id+"F0.wireOp",EDGE,"E28.0.11.0"),sQuery(id+"F0.wireOp",EDGE,"E28.0.12.0"),sQuery(id+"F0.wireOp",EDGE,"E28.0.13.0"),sQuery(id+"F0.wireOp",EDGE,"E28.0.14.0"),sQuery(id+"F0.wireOp",EDGE,"E28.0.15.0"),sQuery(id+"F0.wireOp",EDGE,"E28.0.16.0"),sQuery(id+"F0.wireOp",EDGE,"E28.0.17.0"),sQuery(id+"F0.wireOp",EDGE,"E28.0.18.0"),sQuery(id+"F0.wireOp",EDGE,"E29"),sQuery(id+"F0.wireOp",EDGE,"E30"),sQuery(id+"F0.wireOp",EDGE,"E31"),sQuery(id+"F0.wireOp",EDGE,"E32"),sQuery(id+"F0.wireOp",EDGE,"E36"),sQuery(id+"F0.wireOp",EDGE,"E37.0.1.0"),sQuery(id+"F0.wireOp",EDGE,"E37.0.2.0"),sQuery(id+"F0.wireOp",EDGE,"E37.0.3.0"),sQuery(id+"F0.wireOp",EDGE,"E37.0.4.0"),sQuery(id+"F0.wireOp",EDGE,"E37.0.5.0"),sQuery(id+"F0.wireOp",EDGE,"E37.0.6.0"),sQuery(id+"F0.wireOp",EDGE,"E37.0.7.0"),sQuery(id+"F0.wireOp",EDGE,"E37.0.8.0"),sQuery(id+"F0.wireOp",EDGE,"E37.0.9.0"),sQuery(id+"F0.wireOp",EDGE,"E37.0.10.0"),sQuery(id+"F0.wireOp",EDGE,"E37.0.11.0"),sQuery(id+"F0.wireOp",EDGE,"E37.0.12.0"),sQuery(id+"F0.wireOp",EDGE,"E38"),sQuery(id+"F0.wireOp",EDGE,"E42.0.0.13"),sQuery(id+"F0.wireOp",EDGE,"E59"),sQuery(id+"F0.wireOp",EDGE,"E60"),sQuery(id+"F0.wireOp",EDGE,"E61"),sQuery(id+"F0.wireOp",EDGE,"E62"),sQuery(id+"F0.wireOp",EDGE,"E63"),sQuery(id+"F0.wireOp",EDGE,"E64"),sQuery(id+"F0.wireOp",EDGE,"E65"),sQuery(id+"F0.wireOp",EDGE,"E66"),sQuery(id+"F0.wireOp",EDGE,"E67"),sQuery(id+"F0.wireOp",EDGE,"E68.bottom"),sQuery(id+"F0.wireOp",EDGE,"E68.top"),sQuery(id+"F0.wireOp",EDGE,"E68.left"),sQuery(id+"F0.wireOp",EDGE,"E68.right"),sQuery(id+"F0.wireOp",EDGE,"E69.1.0.0"),sQuery(id+"F0.wireOp",EDGE,"E69.1.0.1"),sQuery(id+"F0.wireOp",EDGE,"E69.1.0.2"),sQuery(id+"F0.wireOp",EDGE,"E69.1.0.3"),sQuery(id+"F0.wireOp",EDGE,"E69.2.0.0"),sQuery(id+"F0.wireOp",EDGE,"E69.2.0.1"),sQuery(id+"F0.wireOp",EDGE,"E69.2.0.2"),sQuery(id+"F0.wireOp",EDGE,"E69.2.0.3"),sQuery(id+"F0.wireOp",EDGE,"E69.3.0.0"),sQuery(id+"F0.wireOp",EDGE,"E69.3.0.1"),sQuery(id+"F0.wireOp",EDGE,"E69.3.0.2"),sQuery(id+"F0.wireOp",EDGE,"E69.3.0.3"),sQuery(id+"F0.wireOp",EDGE,"E69.4.0.0"),sQuery(id+"F0.wireOp",EDGE,"E69.4.0.1"),sQuery(id+"F0.wireOp",EDGE,"E69.4.0.2"),sQuery(id+"F0.wireOp",EDGE,"E69.4.0.3"),sQuery(id+"F0.wireOp",EDGE,"E69.5.0.0"),sQuery(id+"F0.wireOp",EDGE,"E69.5.0.1"),sQuery(id+"F0.wireOp",EDGE,"E69.5.0.2"),sQuery(id+"F0.wireOp",EDGE,"E69.5.0.3")])]});
            var Q2;
            Q2=makeQuery(id+"F20.opExtrude","SWEPT_BODY",BODY,{"disambiguationData":[OSD([sQuery(id+"F19.wireOp",EDGE,"E100.bottom"),sQuery(id+"F19.wireOp",EDGE,"E100.top"),sQuery(id+"F19.wireOp",EDGE,"E100.left"),sQuery(id+"F19.wireOp",EDGE,"E101.bottom"),sQuery(id+"F19.wireOp",EDGE,"E101.top"),sQuery(id+"F19.wireOp",EDGE,"E101.right"),sQuery(id+"F19.wireOp",EDGE,"E102.0.1.0"),sQuery(id+"F19.wireOp",EDGE,"E102.0.1.1"),sQuery(id+"F19.wireOp",EDGE,"E102.0.1.2"),sQuery(id+"F19.wireOp",EDGE,"E102.0.2.0"),sQuery(id+"F19.wireOp",EDGE,"E102.0.2.1"),sQuery(id+"F19.wireOp",EDGE,"E102.0.2.2"),sQuery(id+"F19.wireOp",EDGE,"E102.0.3.0"),sQuery(id+"F19.wireOp",EDGE,"E102.0.3.1"),sQuery(id+"F19.wireOp",EDGE,"E102.0.3.2"),sQuery(id+"F19.wireOp",EDGE,"E103.top"),sQuery(id+"F19.wireOp",EDGE,"E103.left"),sQuery(id+"F19.wireOp",EDGE,"E103.right"),sQuery(id+"F19.wireOp",EDGE,"E104.1.0.0"),sQuery(id+"F19.wireOp",EDGE,"E104.1.0.1"),sQuery(id+"F19.wireOp",EDGE,"E104.1.0.3"),sQuery(id+"F19.wireOp",EDGE,"E104.2.0.0"),sQuery(id+"F19.wireOp",EDGE,"E104.2.0.1"),sQuery(id+"F19.wireOp",EDGE,"E104.2.0.3"),sQuery(id+"F19.wireOp",EDGE,"E105.0.3.0"),sQuery(id+"F19.wireOp",EDGE,"E105.3.3.0"),sQuery(id+"F19.wireOp",EDGE,"E106"),sQuery(id+"F19.wireOp",EDGE,"E107.top"),sQuery(id+"F19.wireOp",EDGE,"E107.right")])]});
            var Q3;
            Q3=makeQuery(id+"F21.opExtrude","SWEPT_BODY",BODY,{"disambiguationData":[OSD([sQuery(id+"F18.wireOp",EDGE,"E89.bottom"),sQuery(id+"F18.wireOp",EDGE,"E89.top"),sQuery(id+"F18.wireOp",EDGE,"E89.left"),sQuery(id+"F18.wireOp",EDGE,"E89.right")])]});
            booleanBodies(context, id + "F23", {"operationType" : BooleanOperationType.SUBTRACTION, "tools" : qUnion([Q0, Q1, Q2]), "targets" : qUnion([Q3]), "keepTools" : true});
        }
        {
            var Q0;
            Q0=makeQuery(id+"F3.opExtrude","SWEPT_FACE",FACE,{"disambiguationData":[OSD([sQuery(id+"F0.wireOp",EDGE,"E0")])]});
            var sketch = newSketch(context, id + "F24", { "sketchPlane" : qUnion([Q0])});
            skArc(sketch, "E108", {"start": v(11, 9) * mm, "mid": v(8, 6) * mm, "end": v(11, 3) * mm});
            skArc(sketch, "E109", {"start": v(20, 6) * mm, "mid": v(19.12, 8.12) * mm, "end": v(17, 9) * mm});
            skLineSegment(sketch, "E110", {"start": v(11, 9) * mm, "end": v(17, 9) * mm});
            skLineSegment(sketch, "E111", {"start": v(11, 3) * mm, "end": v(20, 3) * mm});
            skLineSegment(sketch, "E112", {"start": v(20, 6) * mm, "end": v(20, 3) * mm});
            skCircle(sketch, "E113", {"center": v(11, 16) * mm, "radius": 7 * mm, "construction": true});
            skCircle(sketch, "E114", {"center": v(11, 16) * mm, "radius": 4 * mm});
            skSolve(sketch);
        }
        {
            var Q0;
            {var subQ4=sQuery(id+"F24.wireOp",EDGE,"E108");Q0=makeQuery(id+"F24.imprint","IMPRINT",FACE,{"disambiguationData":[TD([[makeQuery(id+"F24.imprint","IMPRINT",EDGE,{"derivedFrom":subQ4}),1.0]])]});}
            var Q1;
            Q1=makeQuery(id+"F24.imprint","IMPRINT",FACE,{"disambiguationData":[TD([[makeQuery(id+"F24.imprint","IMPRINT",EDGE,{"derivedFrom":sQuery(id+"F24.wireOp",EDGE,"E114")}),1.0]])]});
            extrude(context, id + "F25", {"entities" : qUnion([Q0, Q1]), "operationType" : NewBodyOperationType.REMOVE, "oppositeDirection" : true, "depth" : 3 * mm, "offsetDistance" : 25 * mm});
        }
        {
            var Q0;
            Q0=makeQuery(id+"F1.opExtrude","CAP_FACE",FACE,{"disambiguationData":[OSD([sQuery(id+"F0.wireOp",EDGE,"E0"),sQuery(id+"F0.wireOp",EDGE,"E1"),sQuery(id+"F0.wireOp",EDGE,"E2"),sQuery(id+"F0.wireOp",EDGE,"E3"),sQuery(id+"F0.wireOp",EDGE,"E4"),sQuery(id+"F0.wireOp",EDGE,"E5"),sQuery(id+"F0.wireOp",EDGE,"E6"),sQuery(id+"F0.wireOp",EDGE,"E7"),sQuery(id+"F0.wireOp",EDGE,"E8"),sQuery(id+"F0.wireOp",EDGE,"E11"),sQuery(id+"F0.wireOp",EDGE,"E12"),sQuery(id+"F0.wireOp",EDGE,"E13.filletArc"),sQuery(id+"F0.wireOp",EDGE,"E14.filletArc"),sQuery(id+"F0.wireOp",EDGE,"E15.0"),sQuery(id+"F0.wireOp",EDGE,"E15.1"),sQuery(id+"F0.wireOp",EDGE,"E15.3"),sQuery(id+"F0.wireOp",EDGE,"E15.4"),sQuery(id+"F0.wireOp",EDGE,"E15.5"),sQuery(id+"F0.wireOp",EDGE,"E16"),sQuery(id+"F0.wireOp",EDGE,"E17"),sQuery(id+"F0.wireOp",EDGE,"E19"),sQuery(id+"F0.wireOp",EDGE,"E21"),sQuery(id+"F0.wireOp",EDGE,"E27"),sQuery(id+"F0.wireOp",EDGE,"E28.0.1.0"),sQuery(id+"F0.wireOp",EDGE,"E28.0.2.0"),sQuery(id+"F0.wireOp",EDGE,"E28.0.3.0"),sQuery(id+"F0.wireOp",EDGE,"E28.0.4.0"),sQuery(id+"F0.wireOp",EDGE,"E28.0.5.0"),sQuery(id+"F0.wireOp",EDGE,"E28.0.6.0"),sQuery(id+"F0.wireOp",EDGE,"E28.0.7.0"),sQuery(id+"F0.wireOp",EDGE,"E28.0.8.0"),sQuery(id+"F0.wireOp",EDGE,"E28.0.9.0"),sQuery(id+"F0.wireOp",EDGE,"E28.0.10.0"),sQuery(id+"F0.wireOp",EDGE,"E28.0.11.0"),sQuery(id+"F0.wireOp",EDGE,"E28.0.12.0"),sQuery(id+"F0.wireOp",EDGE,"E28.0.13.0"),sQuery(id+"F0.wireOp",EDGE,"E28.0.14.0"),sQuery(id+"F0.wireOp",EDGE,"E28.0.15.0"),sQuery(id+"F0.wireOp",EDGE,"E28.0.16.0"),sQuery(id+"F0.wireOp",EDGE,"E28.0.17.0"),sQuery(id+"F0.wireOp",EDGE,"E28.0.18.0"),sQuery(id+"F0.wireOp",EDGE,"E29"),sQuery(id+"F0.wireOp",EDGE,"E30"),sQuery(id+"F0.wireOp",EDGE,"E31"),sQuery(id+"F0.wireOp",EDGE,"E32"),sQuery(id+"F0.wireOp",EDGE,"E36"),sQuery(id+"F0.wireOp",EDGE,"E37.0.1.0"),sQuery(id+"F0.wireOp",EDGE,"E37.0.2.0"),sQuery(id+"F0.wireOp",EDGE,"E37.0.3.0"),sQuery(id+"F0.wireOp",EDGE,"E37.0.4.0"),sQuery(id+"F0.wireOp",EDGE,"E37.0.5.0"),sQuery(id+"F0.wireOp",EDGE,"E37.0.6.0"),sQuery(id+"F0.wireOp",EDGE,"E37.0.7.0"),sQuery(id+"F0.wireOp",EDGE,"E37.0.8.0"),sQuery(id+"F0.wireOp",EDGE,"E37.0.9.0"),sQuery(id+"F0.wireOp",EDGE,"E37.0.10.0"),sQuery(id+"F0.wireOp",EDGE,"E37.0.11.0"),sQuery(id+"F0.wireOp",EDGE,"E37.0.12.0"),sQuery(id+"F0.wireOp",EDGE,"E38"),sQuery(id+"F0.wireOp",EDGE,"E42.0.0.13"),sQuery(id+"F0.wireOp",EDGE,"E59"),sQuery(id+"F0.wireOp",EDGE,"E60"),sQuery(id+"F0.wireOp",EDGE,"E61"),sQuery(id+"F0.wireOp",EDGE,"E62"),sQuery(id+"F0.wireOp",EDGE,"E63"),sQuery(id+"F0.wireOp",EDGE,"E64"),sQuery(id+"F0.wireOp",EDGE,"E65"),sQuery(id+"F0.wireOp",EDGE,"E66"),sQuery(id+"F0.wireOp",EDGE,"E67"),sQuery(id+"F0.wireOp",EDGE,"E68.bottom"),sQuery(id+"F0.wireOp",EDGE,"E68.top"),sQuery(id+"F0.wireOp",EDGE,"E68.left"),sQuery(id+"F0.wireOp",EDGE,"E68.right"),sQuery(id+"F0.wireOp",EDGE,"E69.1.0.0"),sQuery(id+"F0.wireOp",EDGE,"E69.1.0.1"),sQuery(id+"F0.wireOp",EDGE,"E69.1.0.2"),sQuery(id+"F0.wireOp",EDGE,"E69.1.0.3"),sQuery(id+"F0.wireOp",EDGE,"E69.2.0.0"),sQuery(id+"F0.wireOp",EDGE,"E69.2.0.1"),sQuery(id+"F0.wireOp",EDGE,"E69.2.0.2"),sQuery(id+"F0.wireOp",EDGE,"E69.2.0.3"),sQuery(id+"F0.wireOp",EDGE,"E69.3.0.0"),sQuery(id+"F0.wireOp",EDGE,"E69.3.0.1"),sQuery(id+"F0.wireOp",EDGE,"E69.3.0.2"),sQuery(id+"F0.wireOp",EDGE,"E69.3.0.3"),sQuery(id+"F0.wireOp",EDGE,"E69.4.0.0"),sQuery(id+"F0.wireOp",EDGE,"E69.4.0.1"),sQuery(id+"F0.wireOp",EDGE,"E69.4.0.2"),sQuery(id+"F0.wireOp",EDGE,"E69.4.0.3"),sQuery(id+"F0.wireOp",EDGE,"E69.5.0.0"),sQuery(id+"F0.wireOp",EDGE,"E69.5.0.1"),sQuery(id+"F0.wireOp",EDGE,"E69.5.0.2"),sQuery(id+"F0.wireOp",EDGE,"E69.5.0.3"),sQuery(id+"F0.wireOp",EDGE,"E70"),sQuery(id+"F0.wireOp",EDGE,"E71")])],"isStart":false});
            var sketch = newSketch(context, id + "F26", { "sketchPlane" : qUnion([Q0])});
            skLineSegment(sketch, "E115", {"start": v(-29.06, 177.3) * mm, "end": v(-74.06, 27.3) * mm});
            skLineSegment(sketch, "E116", {"start": v(-66.4, 17) * mm, "end": v(-11, 17) * mm});
            skLineSegment(sketch, "E117", {"start": v(-3, 25) * mm, "end": v(-3, 175) * mm});
            skLineSegment(sketch, "E118", {"start": v(-11, 183) * mm, "end": v(-21.4, 183) * mm});
            skPoint(sketch, "E119.visualSharp", {"position": v(-27.35, 183) * mm});
            skArc(sketch, "E119.filletArc", {"start": v(-21.4, 183) * mm, "mid": v(-26.17, 181.42) * mm, "end": v(-29.06, 177.3) * mm});
            skPoint(sketch, "E120.visualSharp", {"position": v(-77.15, 17) * mm});
            skArc(sketch, "E120.filletArc", {"start": v(-74.06, 27.3) * mm, "mid": v(-72.82, 20.22) * mm, "end": v(-66.4, 17) * mm});
            skPoint(sketch, "E121.visualSharp", {"position": v(-3, 183) * mm});
            skArc(sketch, "E121.filletArc", {"start": v(-3, 175) * mm, "mid": v(-5.34, 180.66) * mm, "end": v(-11, 183) * mm});
            skPoint(sketch, "E122.visualSharp", {"position": v(-3, 17) * mm});
            skArc(sketch, "E122.filletArc", {"start": v(-11, 17) * mm, "mid": v(-5.34, 19.34) * mm, "end": v(-3, 25) * mm});
            skSolve(sketch);
        }
        {
            var Q0;
            Q0=makeQuery(id+"F26.imprint","IMPRINT",FACE,{"disambiguationData":[TD([[makeQuery(id+"F26.imprint","IMPRINT",EDGE,{"derivedFrom":sQuery(id+"F26.wireOp",EDGE,"E115")}),1.0]])]});
            extrude(context, id + "F27", {"entities" : qUnion([Q0]), "operationType" : NewBodyOperationType.REMOVE, "oppositeDirection" : true, "depth" : 4 * mm, "offsetDistance" : 25 * mm});
        }
    });
